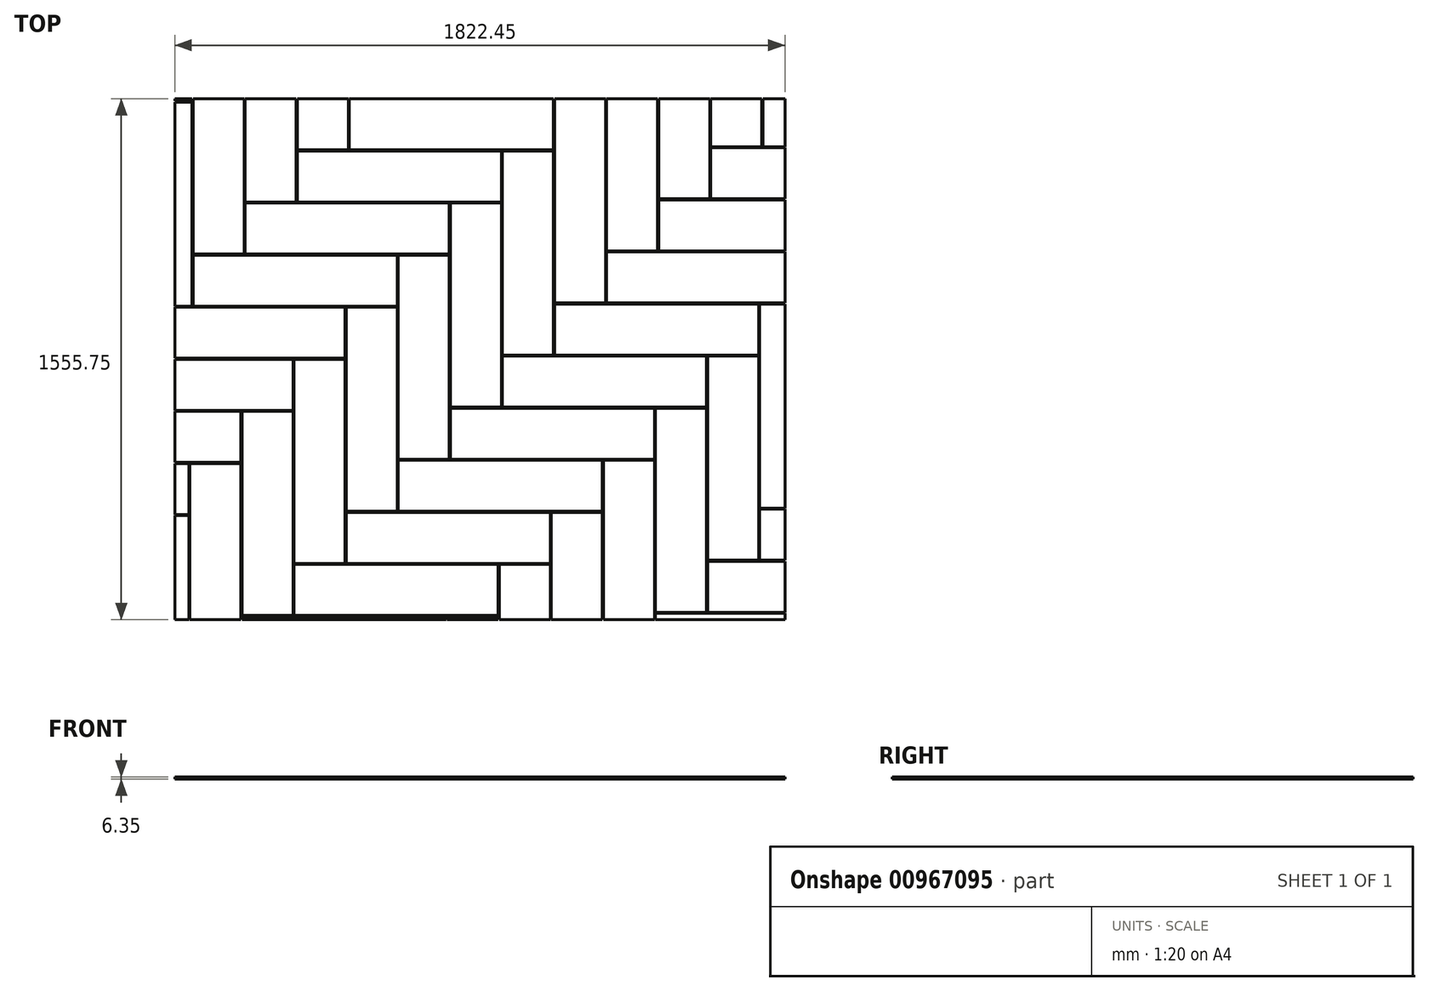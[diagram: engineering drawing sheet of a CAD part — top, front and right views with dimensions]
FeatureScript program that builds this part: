
annotation { "Feature Type Name" : "Feature", "Feature Type Description" : "" }
export const myFeature = defineFeature(function(context is Context, id is Id, definition is map)
    precondition{}
    {
        {
            var Q0;
            Q0=qCreatedBy(makeId("Top.planeOp"),FACE);
            var sketch = newSketch(context, id + "F0", { "sketchPlane" : qUnion([Q0])});
            skLineSegment(sketch, "E0.bottom", {"start": v(0, 0) * mm, "end": v(609.6, 0) * mm});
            skLineSegment(sketch, "E0.top", {"start": v(0, 152.4) * mm, "end": v(609.6, 152.4) * mm});
            skLineSegment(sketch, "E0.left", {"start": v(0, 0) * mm, "end": v(0, 152.4) * mm});
            skLineSegment(sketch, "E0.right", {"start": v(609.6, 0) * mm, "end": v(609.6, 152.4) * mm});
            skLineSegment(sketch, "E1.bottom", {"start": v(152.4, 155.57) * mm, "end": v(152.4, 765.17) * mm});
            skLineSegment(sketch, "E1.top", {"start": v(0, 155.58) * mm, "end": v(0, 765.17) * mm});
            skLineSegment(sketch, "E1.left", {"start": v(152.4, 155.57) * mm, "end": v(0, 155.57) * mm});
            skLineSegment(sketch, "E1.right", {"start": v(152.4, 765.17) * mm, "end": v(0, 765.17) * mm});
            skLineSegment(sketch, "E2.bottom", {"start": v(155.58, 155.57) * mm, "end": v(765.17, 155.57) * mm});
            skLineSegment(sketch, "E2.top", {"start": v(155.58, 307.98) * mm, "end": v(765.17, 307.97) * mm});
            skLineSegment(sketch, "E2.left", {"start": v(155.58, 155.58) * mm, "end": v(155.58, 307.98) * mm});
            skLineSegment(sketch, "E2.right", {"start": v(765.17, 155.57) * mm, "end": v(765.17, 307.97) * mm});
            skLineSegment(sketch, "E3.bottom", {"start": v(307.98, 311.15) * mm, "end": v(307.98, 920.75) * mm});
            skLineSegment(sketch, "E3.top", {"start": v(155.58, 311.15) * mm, "end": v(155.58, 920.75) * mm});
            skLineSegment(sketch, "E3.left", {"start": v(307.98, 311.15) * mm, "end": v(155.58, 311.15) * mm});
            skLineSegment(sketch, "E3.right", {"start": v(307.98, 920.75) * mm, "end": v(155.58, 920.75) * mm});
            skLineSegment(sketch, "E4.0.1.0", {"start": v(-612.78, 612.78) * mm, "end": v(-3.18, 612.78) * mm});
            skLineSegment(sketch, "E4.0.1.1", {"start": v(-460.37, 768.35) * mm, "end": v(-612.77, 768.35) * mm});
            skLineSegment(sketch, "E4.0.1.2", {"start": v(-457.2, 768.35) * mm, "end": v(-457.2, 920.75) * mm});
            skLineSegment(sketch, "E4.0.1.3", {"start": v(-304.8, 923.92) * mm, "end": v(-457.2, 923.92) * mm});
            skLineSegment(sketch, "E4.0.1.4", {"start": v(-457.2, 768.35) * mm, "end": v(152.4, 768.35) * mm});
            skLineSegment(sketch, "E4.0.1.5", {"start": v(-460.37, 768.35) * mm, "end": v(-460.37, 1377.95) * mm});
            skLineSegment(sketch, "E4.0.1.6", {"start": v(-457.2, 920.75) * mm, "end": v(152.4, 920.75) * mm});
            skLineSegment(sketch, "E4.0.1.7", {"start": v(-304.8, 1533.52) * mm, "end": v(-457.2, 1533.52) * mm});
            skLineSegment(sketch, "E4.0.1.8", {"start": v(-612.78, 768.35) * mm, "end": v(-612.77, 1377.95) * mm});
            skLineSegment(sketch, "E4.0.1.9", {"start": v(-457.2, 923.92) * mm, "end": v(-457.2, 1533.52) * mm});
            skLineSegment(sketch, "E4.0.1.10", {"start": v(-3.18, 612.78) * mm, "end": v(-3.18, 765.17) * mm});
            skLineSegment(sketch, "E4.0.1.11", {"start": v(-304.8, 923.92) * mm, "end": v(-304.8, 1533.52) * mm});
            skLineSegment(sketch, "E4.0.1.12", {"start": v(-612.78, 612.78) * mm, "end": v(-612.78, 765.17) * mm});
            skLineSegment(sketch, "E4.0.1.13", {"start": v(-460.37, 1377.95) * mm, "end": v(-612.77, 1377.95) * mm});
            skLineSegment(sketch, "E4.0.1.14", {"start": v(152.4, 768.35) * mm, "end": v(152.4, 920.75) * mm});
            skLineSegment(sketch, "E4.0.1.15", {"start": v(-612.77, 765.17) * mm, "end": v(-3.17, 765.17) * mm});
            skLineSegment(sketch, "E4.1.0.0", {"start": v(311.15, 311.15) * mm, "end": v(920.75, 311.15) * mm});
            skLineSegment(sketch, "E4.1.0.1", {"start": v(463.55, 466.72) * mm, "end": v(311.15, 466.72) * mm});
            skLineSegment(sketch, "E4.1.0.2", {"start": v(466.73, 466.72) * mm, "end": v(466.73, 619.12) * mm});
            skLineSegment(sketch, "E4.1.0.3", {"start": v(619.13, 622.3) * mm, "end": v(466.73, 622.3) * mm});
            skLineSegment(sketch, "E4.1.0.4", {"start": v(466.73, 466.72) * mm, "end": v(1076.33, 466.72) * mm});
            skLineSegment(sketch, "E4.1.0.5", {"start": v(463.55, 466.72) * mm, "end": v(463.55, 1076.32) * mm});
            skLineSegment(sketch, "E4.1.0.6", {"start": v(466.73, 619.12) * mm, "end": v(1076.33, 619.12) * mm});
            skLineSegment(sketch, "E4.1.0.7", {"start": v(619.13, 1231.9) * mm, "end": v(466.73, 1231.9) * mm});
            skLineSegment(sketch, "E4.1.0.8", {"start": v(311.15, 466.72) * mm, "end": v(311.15, 1076.32) * mm});
            skLineSegment(sketch, "E4.1.0.9", {"start": v(466.73, 622.3) * mm, "end": v(466.73, 1231.9) * mm});
            skLineSegment(sketch, "E4.1.0.10", {"start": v(920.75, 311.15) * mm, "end": v(920.75, 463.55) * mm});
            skLineSegment(sketch, "E4.1.0.11", {"start": v(619.13, 622.3) * mm, "end": v(619.13, 1231.9) * mm});
            skLineSegment(sketch, "E4.1.0.12", {"start": v(311.15, 311.15) * mm, "end": v(311.15, 463.55) * mm});
            skLineSegment(sketch, "E4.1.0.13", {"start": v(463.55, 1076.32) * mm, "end": v(311.15, 1076.32) * mm});
            skLineSegment(sketch, "E4.1.0.14", {"start": v(1076.32, 466.72) * mm, "end": v(1076.32, 619.12) * mm});
            skLineSegment(sketch, "E4.1.0.15", {"start": v(311.15, 463.55) * mm, "end": v(920.75, 463.55) * mm});
            skLineSegment(sketch, "E4.1.1.0", {"start": v(-301.62, 923.92) * mm, "end": v(307.98, 923.92) * mm});
            skLineSegment(sketch, "E4.1.1.1", {"start": v(-149.22, 1079.5) * mm, "end": v(-301.62, 1079.5) * mm});
            skLineSegment(sketch, "E4.1.1.2", {"start": v(-146.05, 1079.5) * mm, "end": v(-146.05, 1231.9) * mm});
            skLineSegment(sketch, "E4.1.1.3", {"start": v(6.35, 1235.07) * mm, "end": v(-146.05, 1235.07) * mm});
            skLineSegment(sketch, "E4.1.1.4", {"start": v(-146.05, 1079.5) * mm, "end": v(463.55, 1079.5) * mm});
            skLineSegment(sketch, "E4.1.1.5", {"start": v(-149.22, 1079.5) * mm, "end": v(-149.22, 1689.1) * mm});
            skLineSegment(sketch, "E4.1.1.6", {"start": v(-146.05, 1231.9) * mm, "end": v(463.55, 1231.9) * mm});
            skLineSegment(sketch, "E4.1.1.7", {"start": v(6.35, 1844.67) * mm, "end": v(-146.05, 1844.67) * mm});
            skLineSegment(sketch, "E4.1.1.8", {"start": v(-301.62, 1079.5) * mm, "end": v(-301.62, 1689.1) * mm});
            skLineSegment(sketch, "E4.1.1.9", {"start": v(-146.05, 1235.07) * mm, "end": v(-146.05, 1844.67) * mm});
            skLineSegment(sketch, "E4.1.1.10", {"start": v(307.98, 923.92) * mm, "end": v(307.98, 1076.32) * mm});
            skLineSegment(sketch, "E4.1.1.11", {"start": v(6.35, 1235.07) * mm, "end": v(6.35, 1844.67) * mm});
            skLineSegment(sketch, "E4.1.1.12", {"start": v(-301.62, 923.92) * mm, "end": v(-301.62, 1076.32) * mm});
            skLineSegment(sketch, "E4.1.1.13", {"start": v(-149.22, 1689.1) * mm, "end": v(-301.62, 1689.1) * mm});
            skLineSegment(sketch, "E4.1.1.14", {"start": v(463.55, 1079.5) * mm, "end": v(463.55, 1231.9) * mm});
            skLineSegment(sketch, "E4.1.1.15", {"start": v(-301.62, 1076.32) * mm, "end": v(307.98, 1076.32) * mm});
            skLineSegment(sketch, "E4.2.0.0", {"start": v(622.3, 622.3) * mm, "end": v(1231.9, 622.3) * mm});
            skLineSegment(sketch, "E4.2.0.1", {"start": v(774.7, 777.87) * mm, "end": v(622.3, 777.87) * mm});
            skLineSegment(sketch, "E4.2.0.2", {"start": v(777.88, 777.87) * mm, "end": v(777.88, 930.27) * mm});
            skLineSegment(sketch, "E4.2.0.3", {"start": v(930.28, 933.45) * mm, "end": v(777.88, 933.45) * mm});
            skLineSegment(sketch, "E4.2.0.4", {"start": v(777.88, 777.87) * mm, "end": v(1387.47, 777.87) * mm});
            skLineSegment(sketch, "E4.2.0.5", {"start": v(774.7, 777.87) * mm, "end": v(774.7, 1387.47) * mm});
            skLineSegment(sketch, "E4.2.0.6", {"start": v(777.88, 930.27) * mm, "end": v(1387.47, 930.27) * mm});
            skLineSegment(sketch, "E4.2.0.7", {"start": v(930.28, 1543.05) * mm, "end": v(777.88, 1543.05) * mm});
            skLineSegment(sketch, "E4.2.0.8", {"start": v(622.3, 777.87) * mm, "end": v(622.3, 1387.47) * mm});
            skLineSegment(sketch, "E4.2.0.9", {"start": v(777.88, 933.45) * mm, "end": v(777.88, 1543.05) * mm});
            skLineSegment(sketch, "E4.2.0.10", {"start": v(1231.9, 622.3) * mm, "end": v(1231.9, 774.7) * mm});
            skLineSegment(sketch, "E4.2.0.11", {"start": v(930.28, 933.45) * mm, "end": v(930.28, 1543.05) * mm});
            skLineSegment(sketch, "E4.2.0.12", {"start": v(622.3, 622.3) * mm, "end": v(622.3, 774.7) * mm});
            skLineSegment(sketch, "E4.2.0.13", {"start": v(774.7, 1387.47) * mm, "end": v(622.3, 1387.47) * mm});
            skLineSegment(sketch, "E4.2.0.14", {"start": v(1387.47, 777.87) * mm, "end": v(1387.47, 930.27) * mm});
            skLineSegment(sketch, "E4.2.0.15", {"start": v(622.3, 774.7) * mm, "end": v(1231.9, 774.7) * mm});
            skLineSegment(sketch, "E4.2.1.0", {"start": v(9.53, 1235.07) * mm, "end": v(619.13, 1235.07) * mm});
            skLineSegment(sketch, "E4.2.1.1", {"start": v(161.93, 1390.65) * mm, "end": v(9.53, 1390.65) * mm});
            skLineSegment(sketch, "E4.2.1.2", {"start": v(165.1, 1390.65) * mm, "end": v(165.1, 1543.05) * mm});
            skLineSegment(sketch, "E4.2.1.3", {"start": v(317.5, 1546.22) * mm, "end": v(165.1, 1546.22) * mm});
            skLineSegment(sketch, "E4.2.1.4", {"start": v(165.1, 1390.65) * mm, "end": v(774.7, 1390.65) * mm});
            skLineSegment(sketch, "E4.2.1.5", {"start": v(161.93, 1390.65) * mm, "end": v(161.93, 2000.25) * mm});
            skLineSegment(sketch, "E4.2.1.6", {"start": v(165.1, 1543.05) * mm, "end": v(774.7, 1543.05) * mm});
            skLineSegment(sketch, "E4.2.1.7", {"start": v(317.5, 2155.82) * mm, "end": v(165.1, 2155.82) * mm});
            skLineSegment(sketch, "E4.2.1.8", {"start": v(9.53, 1390.65) * mm, "end": v(9.53, 2000.25) * mm});
            skLineSegment(sketch, "E4.2.1.9", {"start": v(165.1, 1546.22) * mm, "end": v(165.1, 2155.82) * mm});
            skLineSegment(sketch, "E4.2.1.10", {"start": v(619.13, 1235.07) * mm, "end": v(619.13, 1387.47) * mm});
            skLineSegment(sketch, "E4.2.1.11", {"start": v(317.5, 1546.22) * mm, "end": v(317.5, 2155.82) * mm});
            skLineSegment(sketch, "E4.2.1.12", {"start": v(9.53, 1235.07) * mm, "end": v(9.53, 1387.47) * mm});
            skLineSegment(sketch, "E4.2.1.13", {"start": v(161.93, 2000.25) * mm, "end": v(9.53, 2000.25) * mm});
            skLineSegment(sketch, "E4.2.1.14", {"start": v(774.7, 1390.65) * mm, "end": v(774.7, 1543.05) * mm});
            skLineSegment(sketch, "E4.2.1.15", {"start": v(9.53, 1387.47) * mm, "end": v(619.13, 1387.47) * mm});
            skLineSegment(sketch, "E4.direction1", {"start": v(0, 0) * mm, "end": v(311.15, 311.15) * mm, "construction": true});
            skLineSegment(sketch, "E4.direction2", {"start": v(0, 0) * mm, "end": v(-612.78, 612.78) * mm, "construction": true});
            skLineSegment(sketch, "E5.0.3.0", {"start": v(933.45, 933.45) * mm, "end": v(1543.05, 933.45) * mm});
            skLineSegment(sketch, "E5.3.3.0", {"start": v(1085.85, 1089.02) * mm, "end": v(933.45, 1089.02) * mm});
            skLineSegment(sketch, "E5.6.3.0", {"start": v(1089.03, 1089.02) * mm, "end": v(1089.03, 1241.42) * mm});
            skLineSegment(sketch, "E5.9.3.0", {"start": v(1241.43, 1244.6) * mm, "end": v(1089.03, 1244.6) * mm});
            skLineSegment(sketch, "E5.12.3.0", {"start": v(1089.03, 1089.02) * mm, "end": v(1698.62, 1089.02) * mm});
            skLineSegment(sketch, "E5.15.3.0", {"start": v(1085.85, 1089.02) * mm, "end": v(1085.85, 1698.62) * mm});
            skLineSegment(sketch, "E5.18.3.0", {"start": v(1089.03, 1241.42) * mm, "end": v(1698.62, 1241.42) * mm});
            skLineSegment(sketch, "E5.21.3.0", {"start": v(1241.43, 1854.2) * mm, "end": v(1089.03, 1854.2) * mm});
            skLineSegment(sketch, "E5.24.3.0", {"start": v(933.45, 1089.02) * mm, "end": v(933.45, 1698.62) * mm});
            skLineSegment(sketch, "E5.27.3.0", {"start": v(1089.03, 1244.6) * mm, "end": v(1089.03, 1854.2) * mm});
            skLineSegment(sketch, "E5.30.3.0", {"start": v(1543.05, 933.45) * mm, "end": v(1543.05, 1085.85) * mm});
            skLineSegment(sketch, "E5.33.3.0", {"start": v(1241.43, 1244.6) * mm, "end": v(1241.43, 1854.2) * mm});
            skLineSegment(sketch, "E5.36.3.0", {"start": v(933.45, 933.45) * mm, "end": v(933.45, 1085.85) * mm});
            skLineSegment(sketch, "E5.39.3.0", {"start": v(1085.85, 1698.62) * mm, "end": v(933.45, 1698.62) * mm});
            skLineSegment(sketch, "E5.42.3.0", {"start": v(1698.62, 1089.02) * mm, "end": v(1698.62, 1241.42) * mm});
            skLineSegment(sketch, "E5.45.3.0", {"start": v(933.45, 1085.85) * mm, "end": v(1543.05, 1085.85) * mm});
            skLineSegment(sketch, "E5.0.3.1", {"start": v(320.68, 1546.22) * mm, "end": v(930.28, 1546.22) * mm});
            skLineSegment(sketch, "E5.3.3.1", {"start": v(473.08, 1701.8) * mm, "end": v(320.68, 1701.8) * mm});
            skLineSegment(sketch, "E5.6.3.1", {"start": v(476.25, 1701.8) * mm, "end": v(476.25, 1854.2) * mm});
            skLineSegment(sketch, "E5.9.3.1", {"start": v(628.65, 1857.37) * mm, "end": v(476.25, 1857.37) * mm});
            skLineSegment(sketch, "E5.12.3.1", {"start": v(476.25, 1701.8) * mm, "end": v(1085.85, 1701.8) * mm});
            skLineSegment(sketch, "E5.15.3.1", {"start": v(473.08, 1701.8) * mm, "end": v(473.08, 2311.4) * mm});
            skLineSegment(sketch, "E5.18.3.1", {"start": v(476.25, 1854.2) * mm, "end": v(1085.85, 1854.2) * mm});
            skLineSegment(sketch, "E5.21.3.1", {"start": v(628.65, 2466.97) * mm, "end": v(476.25, 2466.97) * mm});
            skLineSegment(sketch, "E5.24.3.1", {"start": v(320.68, 1701.8) * mm, "end": v(320.68, 2311.4) * mm});
            skLineSegment(sketch, "E5.27.3.1", {"start": v(476.25, 1857.37) * mm, "end": v(476.25, 2466.97) * mm});
            skLineSegment(sketch, "E5.30.3.1", {"start": v(930.28, 1546.22) * mm, "end": v(930.28, 1698.62) * mm});
            skLineSegment(sketch, "E5.33.3.1", {"start": v(628.65, 1857.37) * mm, "end": v(628.65, 2466.97) * mm});
            skLineSegment(sketch, "E5.36.3.1", {"start": v(320.68, 1546.22) * mm, "end": v(320.68, 1698.62) * mm});
            skLineSegment(sketch, "E5.39.3.1", {"start": v(473.08, 2311.4) * mm, "end": v(320.68, 2311.4) * mm});
            skLineSegment(sketch, "E5.42.3.1", {"start": v(1085.85, 1701.8) * mm, "end": v(1085.85, 1854.2) * mm});
            skLineSegment(sketch, "E5.45.3.1", {"start": v(320.68, 1698.62) * mm, "end": v(930.28, 1698.62) * mm});
            skLineSegment(sketch, "E5.0.4.0", {"start": v(1244.6, 1244.6) * mm, "end": v(1854.2, 1244.6) * mm});
            skLineSegment(sketch, "E5.3.4.0", {"start": v(1397, 1400.17) * mm, "end": v(1244.6, 1400.17) * mm});
            skLineSegment(sketch, "E5.6.4.0", {"start": v(1400.18, 1400.17) * mm, "end": v(1400.18, 1552.57) * mm});
            skLineSegment(sketch, "E5.9.4.0", {"start": v(1552.58, 1555.75) * mm, "end": v(1400.18, 1555.75) * mm});
            skLineSegment(sketch, "E5.12.4.0", {"start": v(1400.18, 1400.17) * mm, "end": v(2009.78, 1400.17) * mm});
            skLineSegment(sketch, "E5.15.4.0", {"start": v(1397, 1400.17) * mm, "end": v(1397, 2009.77) * mm});
            skLineSegment(sketch, "E5.18.4.0", {"start": v(1400.18, 1552.57) * mm, "end": v(2009.78, 1552.57) * mm});
            skLineSegment(sketch, "E5.21.4.0", {"start": v(1552.58, 2165.35) * mm, "end": v(1400.18, 2165.35) * mm});
            skLineSegment(sketch, "E5.24.4.0", {"start": v(1244.6, 1400.17) * mm, "end": v(1244.6, 2009.77) * mm});
            skLineSegment(sketch, "E5.27.4.0", {"start": v(1400.18, 1555.75) * mm, "end": v(1400.18, 2165.35) * mm});
            skLineSegment(sketch, "E5.30.4.0", {"start": v(1854.2, 1244.6) * mm, "end": v(1854.2, 1397) * mm});
            skLineSegment(sketch, "E5.33.4.0", {"start": v(1552.58, 1555.75) * mm, "end": v(1552.58, 2165.35) * mm});
            skLineSegment(sketch, "E5.36.4.0", {"start": v(1244.6, 1244.6) * mm, "end": v(1244.6, 1397) * mm});
            skLineSegment(sketch, "E5.39.4.0", {"start": v(1397, 2009.77) * mm, "end": v(1244.6, 2009.77) * mm});
            skLineSegment(sketch, "E5.42.4.0", {"start": v(2009.78, 1400.17) * mm, "end": v(2009.78, 1552.57) * mm});
            skLineSegment(sketch, "E5.45.4.0", {"start": v(1244.6, 1397) * mm, "end": v(1854.2, 1397) * mm});
            skLineSegment(sketch, "E5.0.4.1", {"start": v(631.83, 1857.37) * mm, "end": v(1241.43, 1857.37) * mm});
            skLineSegment(sketch, "E5.3.4.1", {"start": v(784.23, 2012.95) * mm, "end": v(631.83, 2012.95) * mm});
            skLineSegment(sketch, "E5.6.4.1", {"start": v(787.4, 2012.95) * mm, "end": v(787.4, 2165.35) * mm});
            skLineSegment(sketch, "E5.9.4.1", {"start": v(939.8, 2168.52) * mm, "end": v(787.4, 2168.52) * mm});
            skLineSegment(sketch, "E5.12.4.1", {"start": v(787.4, 2012.95) * mm, "end": v(1397, 2012.95) * mm});
            skLineSegment(sketch, "E5.15.4.1", {"start": v(784.23, 2012.95) * mm, "end": v(784.23, 2622.55) * mm});
            skLineSegment(sketch, "E5.18.4.1", {"start": v(787.4, 2165.35) * mm, "end": v(1397, 2165.35) * mm});
            skLineSegment(sketch, "E5.21.4.1", {"start": v(939.8, 2778.12) * mm, "end": v(787.4, 2778.12) * mm});
            skLineSegment(sketch, "E5.24.4.1", {"start": v(631.83, 2012.95) * mm, "end": v(631.83, 2622.55) * mm});
            skLineSegment(sketch, "E5.27.4.1", {"start": v(787.4, 2168.52) * mm, "end": v(787.4, 2778.12) * mm});
            skLineSegment(sketch, "E5.30.4.1", {"start": v(1241.43, 1857.37) * mm, "end": v(1241.43, 2009.77) * mm});
            skLineSegment(sketch, "E5.33.4.1", {"start": v(939.8, 2168.52) * mm, "end": v(939.8, 2778.12) * mm});
            skLineSegment(sketch, "E5.36.4.1", {"start": v(631.83, 1857.37) * mm, "end": v(631.83, 2009.77) * mm});
            skLineSegment(sketch, "E5.39.4.1", {"start": v(784.23, 2622.55) * mm, "end": v(631.83, 2622.55) * mm});
            skLineSegment(sketch, "E5.42.4.1", {"start": v(1397, 2012.95) * mm, "end": v(1397, 2165.35) * mm});
            skLineSegment(sketch, "E5.45.4.1", {"start": v(631.83, 2009.77) * mm, "end": v(1241.43, 2009.77) * mm});
            skLineSegment(sketch, "E5.0.5.0", {"start": v(1555.75, 1555.75) * mm, "end": v(2165.35, 1555.75) * mm});
            skLineSegment(sketch, "E5.3.5.0", {"start": v(1708.15, 1711.32) * mm, "end": v(1555.75, 1711.32) * mm});
            skLineSegment(sketch, "E5.6.5.0", {"start": v(1711.33, 1711.32) * mm, "end": v(1711.33, 1863.72) * mm});
            skLineSegment(sketch, "E5.9.5.0", {"start": v(1863.73, 1866.9) * mm, "end": v(1711.33, 1866.9) * mm});
            skLineSegment(sketch, "E5.12.5.0", {"start": v(1711.33, 1711.32) * mm, "end": v(2320.92, 1711.32) * mm});
            skLineSegment(sketch, "E5.15.5.0", {"start": v(1708.15, 1711.32) * mm, "end": v(1708.15, 2320.92) * mm});
            skLineSegment(sketch, "E5.18.5.0", {"start": v(1711.33, 1863.72) * mm, "end": v(2320.92, 1863.72) * mm});
            skLineSegment(sketch, "E5.21.5.0", {"start": v(1863.73, 2476.5) * mm, "end": v(1711.33, 2476.5) * mm});
            skLineSegment(sketch, "E5.24.5.0", {"start": v(1555.75, 1711.32) * mm, "end": v(1555.75, 2320.92) * mm});
            skLineSegment(sketch, "E5.27.5.0", {"start": v(1711.33, 1866.9) * mm, "end": v(1711.33, 2476.5) * mm});
            skLineSegment(sketch, "E5.30.5.0", {"start": v(2165.35, 1555.75) * mm, "end": v(2165.35, 1708.15) * mm});
            skLineSegment(sketch, "E5.33.5.0", {"start": v(1863.73, 1866.9) * mm, "end": v(1863.73, 2476.5) * mm});
            skLineSegment(sketch, "E5.36.5.0", {"start": v(1555.75, 1555.75) * mm, "end": v(1555.75, 1708.15) * mm});
            skLineSegment(sketch, "E5.39.5.0", {"start": v(1708.15, 2320.92) * mm, "end": v(1555.75, 2320.92) * mm});
            skLineSegment(sketch, "E5.42.5.0", {"start": v(2320.92, 1711.32) * mm, "end": v(2320.92, 1863.72) * mm});
            skLineSegment(sketch, "E5.45.5.0", {"start": v(1555.75, 1708.15) * mm, "end": v(2165.35, 1708.15) * mm});
            skLineSegment(sketch, "E5.0.5.1", {"start": v(942.98, 2168.52) * mm, "end": v(1552.58, 2168.52) * mm});
            skLineSegment(sketch, "E5.3.5.1", {"start": v(1095.38, 2324.1) * mm, "end": v(942.98, 2324.1) * mm});
            skLineSegment(sketch, "E5.6.5.1", {"start": v(1098.55, 2324.1) * mm, "end": v(1098.55, 2476.5) * mm});
            skLineSegment(sketch, "E5.9.5.1", {"start": v(1250.95, 2479.67) * mm, "end": v(1098.55, 2479.67) * mm});
            skLineSegment(sketch, "E5.12.5.1", {"start": v(1098.55, 2324.1) * mm, "end": v(1708.15, 2324.1) * mm});
            skLineSegment(sketch, "E5.15.5.1", {"start": v(1095.38, 2324.1) * mm, "end": v(1095.38, 2933.7) * mm});
            skLineSegment(sketch, "E5.18.5.1", {"start": v(1098.55, 2476.5) * mm, "end": v(1708.15, 2476.5) * mm});
            skLineSegment(sketch, "E5.21.5.1", {"start": v(1250.95, 3089.27) * mm, "end": v(1098.55, 3089.27) * mm});
            skLineSegment(sketch, "E5.24.5.1", {"start": v(942.98, 2324.1) * mm, "end": v(942.98, 2933.7) * mm});
            skLineSegment(sketch, "E5.27.5.1", {"start": v(1098.55, 2479.67) * mm, "end": v(1098.55, 3089.27) * mm});
            skLineSegment(sketch, "E5.30.5.1", {"start": v(1552.58, 2168.52) * mm, "end": v(1552.58, 2320.92) * mm});
            skLineSegment(sketch, "E5.33.5.1", {"start": v(1250.95, 2479.67) * mm, "end": v(1250.95, 3089.27) * mm});
            skLineSegment(sketch, "E5.36.5.1", {"start": v(942.98, 2168.52) * mm, "end": v(942.98, 2320.92) * mm});
            skLineSegment(sketch, "E5.39.5.1", {"start": v(1095.38, 2933.7) * mm, "end": v(942.98, 2933.7) * mm});
            skLineSegment(sketch, "E5.42.5.1", {"start": v(1708.15, 2324.1) * mm, "end": v(1708.15, 2476.5) * mm});
            skLineSegment(sketch, "E5.45.5.1", {"start": v(942.98, 2320.92) * mm, "end": v(1552.58, 2320.92) * mm});
            skLineSegment(sketch, "E6.0.0.2", {"start": v(-1225.55, 1225.55) * mm, "end": v(-615.95, 1225.55) * mm});
            skLineSegment(sketch, "E6.3.0.2", {"start": v(-1073.15, 1381.12) * mm, "end": v(-1225.55, 1381.12) * mm});
            skLineSegment(sketch, "E6.6.0.2", {"start": v(-1069.97, 1381.12) * mm, "end": v(-1069.97, 1533.52) * mm});
            skLineSegment(sketch, "E6.9.0.2", {"start": v(-917.57, 1536.7) * mm, "end": v(-1069.97, 1536.7) * mm});
            skLineSegment(sketch, "E6.12.0.2", {"start": v(-1069.97, 1381.12) * mm, "end": v(-460.37, 1381.12) * mm});
            skLineSegment(sketch, "E6.15.0.2", {"start": v(-1073.15, 1381.12) * mm, "end": v(-1073.15, 1990.72) * mm});
            skLineSegment(sketch, "E6.18.0.2", {"start": v(-1069.97, 1533.52) * mm, "end": v(-460.37, 1533.52) * mm});
            skLineSegment(sketch, "E6.21.0.2", {"start": v(-917.57, 2146.3) * mm, "end": v(-1069.97, 2146.3) * mm});
            skLineSegment(sketch, "E6.24.0.2", {"start": v(-1225.55, 1381.12) * mm, "end": v(-1225.55, 1990.72) * mm});
            skLineSegment(sketch, "E6.27.0.2", {"start": v(-1069.97, 1536.7) * mm, "end": v(-1069.97, 2146.3) * mm});
            skLineSegment(sketch, "E6.30.0.2", {"start": v(-615.95, 1225.55) * mm, "end": v(-615.95, 1377.95) * mm});
            skLineSegment(sketch, "E6.33.0.2", {"start": v(-917.57, 1536.7) * mm, "end": v(-917.57, 2146.3) * mm});
            skLineSegment(sketch, "E6.36.0.2", {"start": v(-1225.55, 1225.55) * mm, "end": v(-1225.55, 1377.95) * mm});
            skLineSegment(sketch, "E6.39.0.2", {"start": v(-1073.15, 1990.72) * mm, "end": v(-1225.55, 1990.72) * mm});
            skLineSegment(sketch, "E6.42.0.2", {"start": v(-460.37, 1381.12) * mm, "end": v(-460.37, 1533.52) * mm});
            skLineSegment(sketch, "E6.45.0.2", {"start": v(-1225.55, 1377.95) * mm, "end": v(-615.95, 1377.95) * mm});
            skLineSegment(sketch, "E6.0.0.3", {"start": v(-1838.33, 1838.33) * mm, "end": v(-1228.73, 1838.33) * mm});
            skLineSegment(sketch, "E6.3.0.3", {"start": v(-1685.92, 1993.9) * mm, "end": v(-1838.32, 1993.9) * mm});
            skLineSegment(sketch, "E6.6.0.3", {"start": v(-1682.75, 1993.9) * mm, "end": v(-1682.75, 2146.3) * mm});
            skLineSegment(sketch, "E6.9.0.3", {"start": v(-1530.35, 2149.47) * mm, "end": v(-1682.75, 2149.47) * mm});
            skLineSegment(sketch, "E6.12.0.3", {"start": v(-1682.75, 1993.9) * mm, "end": v(-1073.15, 1993.9) * mm});
            skLineSegment(sketch, "E6.15.0.3", {"start": v(-1685.92, 1993.9) * mm, "end": v(-1685.92, 2603.5) * mm});
            skLineSegment(sketch, "E6.18.0.3", {"start": v(-1682.75, 2146.3) * mm, "end": v(-1073.15, 2146.3) * mm});
            skLineSegment(sketch, "E6.21.0.3", {"start": v(-1530.35, 2759.07) * mm, "end": v(-1682.75, 2759.07) * mm});
            skLineSegment(sketch, "E6.24.0.3", {"start": v(-1838.33, 1993.9) * mm, "end": v(-1838.33, 2603.5) * mm});
            skLineSegment(sketch, "E6.27.0.3", {"start": v(-1682.75, 2149.47) * mm, "end": v(-1682.75, 2759.07) * mm});
            skLineSegment(sketch, "E6.30.0.3", {"start": v(-1228.73, 1838.33) * mm, "end": v(-1228.73, 1990.72) * mm});
            skLineSegment(sketch, "E6.33.0.3", {"start": v(-1530.35, 2149.47) * mm, "end": v(-1530.35, 2759.07) * mm});
            skLineSegment(sketch, "E6.36.0.3", {"start": v(-1838.33, 1838.33) * mm, "end": v(-1838.33, 1990.72) * mm});
            skLineSegment(sketch, "E6.39.0.3", {"start": v(-1685.92, 2603.5) * mm, "end": v(-1838.32, 2603.5) * mm});
            skLineSegment(sketch, "E6.42.0.3", {"start": v(-1073.15, 1993.9) * mm, "end": v(-1073.15, 2146.3) * mm});
            skLineSegment(sketch, "E6.45.0.3", {"start": v(-1838.32, 1990.72) * mm, "end": v(-1228.72, 1990.72) * mm});
            skLineSegment(sketch, "E6.0.0.4", {"start": v(-2451.1, 2451.1) * mm, "end": v(-1841.5, 2451.1) * mm});
            skLineSegment(sketch, "E6.3.0.4", {"start": v(-2298.7, 2606.67) * mm, "end": v(-2451.1, 2606.67) * mm});
            skLineSegment(sketch, "E6.6.0.4", {"start": v(-2295.52, 2606.67) * mm, "end": v(-2295.52, 2759.07) * mm});
            skLineSegment(sketch, "E6.9.0.4", {"start": v(-2143.12, 2762.25) * mm, "end": v(-2295.52, 2762.25) * mm});
            skLineSegment(sketch, "E6.12.0.4", {"start": v(-2295.52, 2606.67) * mm, "end": v(-1685.92, 2606.67) * mm});
            skLineSegment(sketch, "E6.15.0.4", {"start": v(-2298.7, 2606.67) * mm, "end": v(-2298.7, 3216.27) * mm});
            skLineSegment(sketch, "E6.18.0.4", {"start": v(-2295.52, 2759.07) * mm, "end": v(-1685.92, 2759.07) * mm});
            skLineSegment(sketch, "E6.21.0.4", {"start": v(-2143.12, 3371.85) * mm, "end": v(-2295.52, 3371.85) * mm});
            skLineSegment(sketch, "E6.24.0.4", {"start": v(-2451.1, 2606.67) * mm, "end": v(-2451.1, 3216.27) * mm});
            skLineSegment(sketch, "E6.27.0.4", {"start": v(-2295.52, 2762.25) * mm, "end": v(-2295.52, 3371.85) * mm});
            skLineSegment(sketch, "E6.30.0.4", {"start": v(-1841.5, 2451.1) * mm, "end": v(-1841.5, 2603.5) * mm});
            skLineSegment(sketch, "E6.33.0.4", {"start": v(-2143.12, 2762.25) * mm, "end": v(-2143.12, 3371.85) * mm});
            skLineSegment(sketch, "E6.36.0.4", {"start": v(-2451.1, 2451.1) * mm, "end": v(-2451.1, 2603.5) * mm});
            skLineSegment(sketch, "E6.39.0.4", {"start": v(-2298.7, 3216.27) * mm, "end": v(-2451.1, 3216.27) * mm});
            skLineSegment(sketch, "E6.42.0.4", {"start": v(-1685.92, 2606.67) * mm, "end": v(-1685.92, 2759.07) * mm});
            skLineSegment(sketch, "E6.45.0.4", {"start": v(-2451.1, 2603.5) * mm, "end": v(-1841.5, 2603.5) * mm});
            skLineSegment(sketch, "E6.0.1.2", {"start": v(-914.4, 1536.7) * mm, "end": v(-304.8, 1536.7) * mm});
            skLineSegment(sketch, "E6.3.1.2", {"start": v(-762, 1692.27) * mm, "end": v(-914.4, 1692.27) * mm});
            skLineSegment(sketch, "E6.6.1.2", {"start": v(-758.82, 1692.27) * mm, "end": v(-758.82, 1844.67) * mm});
            skLineSegment(sketch, "E6.9.1.2", {"start": v(-606.42, 1847.85) * mm, "end": v(-758.82, 1847.85) * mm});
            skLineSegment(sketch, "E6.12.1.2", {"start": v(-758.82, 1692.27) * mm, "end": v(-149.22, 1692.27) * mm});
            skLineSegment(sketch, "E6.15.1.2", {"start": v(-762, 1692.27) * mm, "end": v(-762, 2301.87) * mm});
            skLineSegment(sketch, "E6.18.1.2", {"start": v(-758.82, 1844.67) * mm, "end": v(-149.22, 1844.67) * mm});
            skLineSegment(sketch, "E6.21.1.2", {"start": v(-606.42, 2457.45) * mm, "end": v(-758.82, 2457.45) * mm});
            skLineSegment(sketch, "E6.24.1.2", {"start": v(-914.4, 1692.27) * mm, "end": v(-914.4, 2301.87) * mm});
            skLineSegment(sketch, "E6.27.1.2", {"start": v(-758.82, 1847.85) * mm, "end": v(-758.82, 2457.45) * mm});
            skLineSegment(sketch, "E6.30.1.2", {"start": v(-304.8, 1536.7) * mm, "end": v(-304.8, 1689.1) * mm});
            skLineSegment(sketch, "E6.33.1.2", {"start": v(-606.42, 1847.85) * mm, "end": v(-606.42, 2457.45) * mm});
            skLineSegment(sketch, "E6.36.1.2", {"start": v(-914.4, 1536.7) * mm, "end": v(-914.4, 1689.1) * mm});
            skLineSegment(sketch, "E6.39.1.2", {"start": v(-762, 2301.87) * mm, "end": v(-914.4, 2301.87) * mm});
            skLineSegment(sketch, "E6.42.1.2", {"start": v(-149.22, 1692.27) * mm, "end": v(-149.22, 1844.67) * mm});
            skLineSegment(sketch, "E6.45.1.2", {"start": v(-914.4, 1689.1) * mm, "end": v(-304.8, 1689.1) * mm});
            skLineSegment(sketch, "E6.0.1.3", {"start": v(-1527.17, 2149.47) * mm, "end": v(-917.57, 2149.47) * mm});
            skLineSegment(sketch, "E6.3.1.3", {"start": v(-1374.77, 2305.05) * mm, "end": v(-1527.17, 2305.05) * mm});
            skLineSegment(sketch, "E6.6.1.3", {"start": v(-1371.6, 2305.05) * mm, "end": v(-1371.6, 2457.45) * mm});
            skLineSegment(sketch, "E6.9.1.3", {"start": v(-1219.2, 2460.62) * mm, "end": v(-1371.6, 2460.62) * mm});
            skLineSegment(sketch, "E6.12.1.3", {"start": v(-1371.6, 2305.05) * mm, "end": v(-762, 2305.05) * mm});
            skLineSegment(sketch, "E6.15.1.3", {"start": v(-1374.77, 2305.05) * mm, "end": v(-1374.77, 2914.65) * mm});
            skLineSegment(sketch, "E6.18.1.3", {"start": v(-1371.6, 2457.45) * mm, "end": v(-762, 2457.45) * mm});
            skLineSegment(sketch, "E6.21.1.3", {"start": v(-1219.2, 3070.22) * mm, "end": v(-1371.6, 3070.22) * mm});
            skLineSegment(sketch, "E6.24.1.3", {"start": v(-1527.17, 2305.05) * mm, "end": v(-1527.17, 2914.65) * mm});
            skLineSegment(sketch, "E6.27.1.3", {"start": v(-1371.6, 2460.62) * mm, "end": v(-1371.6, 3070.22) * mm});
            skLineSegment(sketch, "E6.30.1.3", {"start": v(-917.57, 2149.47) * mm, "end": v(-917.57, 2301.87) * mm});
            skLineSegment(sketch, "E6.33.1.3", {"start": v(-1219.2, 2460.62) * mm, "end": v(-1219.2, 3070.22) * mm});
            skLineSegment(sketch, "E6.36.1.3", {"start": v(-1527.17, 2149.47) * mm, "end": v(-1527.17, 2301.87) * mm});
            skLineSegment(sketch, "E6.39.1.3", {"start": v(-1374.77, 2914.65) * mm, "end": v(-1527.17, 2914.65) * mm});
            skLineSegment(sketch, "E6.42.1.3", {"start": v(-762, 2305.05) * mm, "end": v(-762, 2457.45) * mm});
            skLineSegment(sketch, "E6.45.1.3", {"start": v(-1527.17, 2301.87) * mm, "end": v(-917.57, 2301.87) * mm});
            skLineSegment(sketch, "E6.0.1.4", {"start": v(-2139.95, 2762.25) * mm, "end": v(-1530.35, 2762.25) * mm});
            skLineSegment(sketch, "E6.3.1.4", {"start": v(-1987.55, 2917.82) * mm, "end": v(-2139.95, 2917.82) * mm});
            skLineSegment(sketch, "E6.6.1.4", {"start": v(-1984.37, 2917.82) * mm, "end": v(-1984.37, 3070.22) * mm});
            skLineSegment(sketch, "E6.9.1.4", {"start": v(-1831.97, 3073.4) * mm, "end": v(-1984.37, 3073.4) * mm});
            skLineSegment(sketch, "E6.12.1.4", {"start": v(-1984.37, 2917.82) * mm, "end": v(-1374.77, 2917.82) * mm});
            skLineSegment(sketch, "E6.15.1.4", {"start": v(-1987.55, 2917.82) * mm, "end": v(-1987.55, 3527.42) * mm});
            skLineSegment(sketch, "E6.18.1.4", {"start": v(-1984.37, 3070.22) * mm, "end": v(-1374.77, 3070.22) * mm});
            skLineSegment(sketch, "E6.21.1.4", {"start": v(-1831.97, 3683) * mm, "end": v(-1984.37, 3683) * mm});
            skLineSegment(sketch, "E6.24.1.4", {"start": v(-2139.95, 2917.82) * mm, "end": v(-2139.95, 3527.42) * mm});
            skLineSegment(sketch, "E6.27.1.4", {"start": v(-1984.37, 3073.4) * mm, "end": v(-1984.37, 3683) * mm});
            skLineSegment(sketch, "E6.30.1.4", {"start": v(-1530.35, 2762.25) * mm, "end": v(-1530.35, 2914.65) * mm});
            skLineSegment(sketch, "E6.33.1.4", {"start": v(-1831.97, 3073.4) * mm, "end": v(-1831.97, 3683) * mm});
            skLineSegment(sketch, "E6.36.1.4", {"start": v(-2139.95, 2762.25) * mm, "end": v(-2139.95, 2914.65) * mm});
            skLineSegment(sketch, "E6.39.1.4", {"start": v(-1987.55, 3527.42) * mm, "end": v(-2139.95, 3527.42) * mm});
            skLineSegment(sketch, "E6.42.1.4", {"start": v(-1374.77, 2917.82) * mm, "end": v(-1374.77, 3070.22) * mm});
            skLineSegment(sketch, "E6.45.1.4", {"start": v(-2139.95, 2914.65) * mm, "end": v(-1530.35, 2914.65) * mm});
            skLineSegment(sketch, "E6.0.2.2", {"start": v(-603.25, 1847.85) * mm, "end": v(6.35, 1847.85) * mm});
            skLineSegment(sketch, "E6.3.2.2", {"start": v(-450.85, 2003.42) * mm, "end": v(-603.25, 2003.42) * mm});
            skLineSegment(sketch, "E6.6.2.2", {"start": v(-447.67, 2003.42) * mm, "end": v(-447.67, 2155.82) * mm});
            skLineSegment(sketch, "E6.9.2.2", {"start": v(-295.27, 2159) * mm, "end": v(-447.67, 2159) * mm});
            skLineSegment(sketch, "E6.12.2.2", {"start": v(-447.67, 2003.42) * mm, "end": v(161.93, 2003.42) * mm});
            skLineSegment(sketch, "E6.15.2.2", {"start": v(-450.85, 2003.42) * mm, "end": v(-450.85, 2613.02) * mm});
            skLineSegment(sketch, "E6.18.2.2", {"start": v(-447.67, 2155.82) * mm, "end": v(161.93, 2155.82) * mm});
            skLineSegment(sketch, "E6.21.2.2", {"start": v(-295.27, 2768.6) * mm, "end": v(-447.67, 2768.6) * mm});
            skLineSegment(sketch, "E6.24.2.2", {"start": v(-603.25, 2003.42) * mm, "end": v(-603.25, 2613.02) * mm});
            skLineSegment(sketch, "E6.27.2.2", {"start": v(-447.67, 2159) * mm, "end": v(-447.67, 2768.6) * mm});
            skLineSegment(sketch, "E6.30.2.2", {"start": v(6.35, 1847.85) * mm, "end": v(6.35, 2000.25) * mm});
            skLineSegment(sketch, "E6.33.2.2", {"start": v(-295.27, 2159) * mm, "end": v(-295.27, 2768.6) * mm});
            skLineSegment(sketch, "E6.36.2.2", {"start": v(-603.25, 1847.85) * mm, "end": v(-603.25, 2000.25) * mm});
            skLineSegment(sketch, "E6.39.2.2", {"start": v(-450.85, 2613.02) * mm, "end": v(-603.25, 2613.02) * mm});
            skLineSegment(sketch, "E6.42.2.2", {"start": v(161.93, 2003.42) * mm, "end": v(161.93, 2155.82) * mm});
            skLineSegment(sketch, "E6.45.2.2", {"start": v(-603.25, 2000.25) * mm, "end": v(6.35, 2000.25) * mm});
            skLineSegment(sketch, "E6.0.2.3", {"start": v(-1216.02, 2460.62) * mm, "end": v(-606.42, 2460.62) * mm});
            skLineSegment(sketch, "E6.3.2.3", {"start": v(-1063.62, 2616.2) * mm, "end": v(-1216.02, 2616.2) * mm});
            skLineSegment(sketch, "E6.6.2.3", {"start": v(-1060.45, 2616.2) * mm, "end": v(-1060.45, 2768.6) * mm});
            skLineSegment(sketch, "E6.9.2.3", {"start": v(-908.05, 2771.77) * mm, "end": v(-1060.45, 2771.77) * mm});
            skLineSegment(sketch, "E6.12.2.3", {"start": v(-1060.45, 2616.2) * mm, "end": v(-450.85, 2616.2) * mm});
            skLineSegment(sketch, "E6.15.2.3", {"start": v(-1063.62, 2616.2) * mm, "end": v(-1063.62, 3225.8) * mm});
            skLineSegment(sketch, "E6.18.2.3", {"start": v(-1060.45, 2768.6) * mm, "end": v(-450.85, 2768.6) * mm});
            skLineSegment(sketch, "E6.21.2.3", {"start": v(-908.05, 3381.37) * mm, "end": v(-1060.45, 3381.37) * mm});
            skLineSegment(sketch, "E6.24.2.3", {"start": v(-1216.02, 2616.2) * mm, "end": v(-1216.02, 3225.8) * mm});
            skLineSegment(sketch, "E6.27.2.3", {"start": v(-1060.45, 2771.77) * mm, "end": v(-1060.45, 3381.37) * mm});
            skLineSegment(sketch, "E6.30.2.3", {"start": v(-606.42, 2460.62) * mm, "end": v(-606.42, 2613.02) * mm});
            skLineSegment(sketch, "E6.33.2.3", {"start": v(-908.05, 2771.77) * mm, "end": v(-908.05, 3381.37) * mm});
            skLineSegment(sketch, "E6.36.2.3", {"start": v(-1216.02, 2460.62) * mm, "end": v(-1216.02, 2613.02) * mm});
            skLineSegment(sketch, "E6.39.2.3", {"start": v(-1063.62, 3225.8) * mm, "end": v(-1216.02, 3225.8) * mm});
            skLineSegment(sketch, "E6.42.2.3", {"start": v(-450.85, 2616.2) * mm, "end": v(-450.85, 2768.6) * mm});
            skLineSegment(sketch, "E6.45.2.3", {"start": v(-1216.02, 2613.02) * mm, "end": v(-606.42, 2613.02) * mm});
            skLineSegment(sketch, "E6.0.2.4", {"start": v(-1828.8, 3073.4) * mm, "end": v(-1219.2, 3073.4) * mm});
            skLineSegment(sketch, "E6.3.2.4", {"start": v(-1676.4, 3228.97) * mm, "end": v(-1828.8, 3228.97) * mm});
            skLineSegment(sketch, "E6.6.2.4", {"start": v(-1673.22, 3228.97) * mm, "end": v(-1673.22, 3381.37) * mm});
            skLineSegment(sketch, "E6.9.2.4", {"start": v(-1520.82, 3384.55) * mm, "end": v(-1673.22, 3384.55) * mm});
            skLineSegment(sketch, "E6.12.2.4", {"start": v(-1673.22, 3228.97) * mm, "end": v(-1063.62, 3228.97) * mm});
            skLineSegment(sketch, "E6.15.2.4", {"start": v(-1676.4, 3228.97) * mm, "end": v(-1676.4, 3838.57) * mm});
            skLineSegment(sketch, "E6.18.2.4", {"start": v(-1673.22, 3381.37) * mm, "end": v(-1063.62, 3381.37) * mm});
            skLineSegment(sketch, "E6.21.2.4", {"start": v(-1520.82, 3994.15) * mm, "end": v(-1673.22, 3994.15) * mm});
            skLineSegment(sketch, "E6.24.2.4", {"start": v(-1828.8, 3228.97) * mm, "end": v(-1828.8, 3838.57) * mm});
            skLineSegment(sketch, "E6.27.2.4", {"start": v(-1673.22, 3384.55) * mm, "end": v(-1673.22, 3994.15) * mm});
            skLineSegment(sketch, "E6.30.2.4", {"start": v(-1219.2, 3073.4) * mm, "end": v(-1219.2, 3225.8) * mm});
            skLineSegment(sketch, "E6.33.2.4", {"start": v(-1520.82, 3384.55) * mm, "end": v(-1520.82, 3994.15) * mm});
            skLineSegment(sketch, "E6.36.2.4", {"start": v(-1828.8, 3073.4) * mm, "end": v(-1828.8, 3225.8) * mm});
            skLineSegment(sketch, "E6.39.2.4", {"start": v(-1676.4, 3838.57) * mm, "end": v(-1828.8, 3838.57) * mm});
            skLineSegment(sketch, "E6.42.2.4", {"start": v(-1063.62, 3228.97) * mm, "end": v(-1063.62, 3381.37) * mm});
            skLineSegment(sketch, "E6.45.2.4", {"start": v(-1828.8, 3225.8) * mm, "end": v(-1219.2, 3225.8) * mm});
            skLineSegment(sketch, "E6.0.3.2", {"start": v(-292.1, 2159) * mm, "end": v(317.5, 2159) * mm});
            skLineSegment(sketch, "E6.3.3.2", {"start": v(-139.7, 2314.57) * mm, "end": v(-292.1, 2314.57) * mm});
            skLineSegment(sketch, "E6.6.3.2", {"start": v(-136.52, 2314.57) * mm, "end": v(-136.52, 2466.97) * mm});
            skLineSegment(sketch, "E6.9.3.2", {"start": v(15.88, 2470.15) * mm, "end": v(-136.52, 2470.15) * mm});
            skLineSegment(sketch, "E6.12.3.2", {"start": v(-136.52, 2314.57) * mm, "end": v(473.08, 2314.57) * mm});
            skLineSegment(sketch, "E6.15.3.2", {"start": v(-139.7, 2314.57) * mm, "end": v(-139.7, 2924.17) * mm});
            skLineSegment(sketch, "E6.18.3.2", {"start": v(-136.52, 2466.97) * mm, "end": v(473.08, 2466.97) * mm});
            skLineSegment(sketch, "E6.21.3.2", {"start": v(15.88, 3079.75) * mm, "end": v(-136.52, 3079.75) * mm});
            skLineSegment(sketch, "E6.24.3.2", {"start": v(-292.1, 2314.57) * mm, "end": v(-292.1, 2924.17) * mm});
            skLineSegment(sketch, "E6.27.3.2", {"start": v(-136.52, 2470.15) * mm, "end": v(-136.52, 3079.75) * mm});
            skLineSegment(sketch, "E6.30.3.2", {"start": v(317.5, 2159) * mm, "end": v(317.5, 2311.4) * mm});
            skLineSegment(sketch, "E6.33.3.2", {"start": v(15.88, 2470.15) * mm, "end": v(15.88, 3079.75) * mm});
            skLineSegment(sketch, "E6.36.3.2", {"start": v(-292.1, 2159) * mm, "end": v(-292.1, 2311.4) * mm});
            skLineSegment(sketch, "E6.39.3.2", {"start": v(-139.7, 2924.17) * mm, "end": v(-292.1, 2924.17) * mm});
            skLineSegment(sketch, "E6.42.3.2", {"start": v(473.08, 2314.57) * mm, "end": v(473.08, 2466.97) * mm});
            skLineSegment(sketch, "E6.45.3.2", {"start": v(-292.1, 2311.4) * mm, "end": v(317.5, 2311.4) * mm});
            skLineSegment(sketch, "E6.0.3.3", {"start": v(-904.87, 2771.77) * mm, "end": v(-295.27, 2771.77) * mm});
            skLineSegment(sketch, "E6.3.3.3", {"start": v(-752.47, 2927.35) * mm, "end": v(-904.87, 2927.35) * mm});
            skLineSegment(sketch, "E6.6.3.3", {"start": v(-749.3, 2927.35) * mm, "end": v(-749.3, 3079.75) * mm});
            skLineSegment(sketch, "E6.9.3.3", {"start": v(-596.9, 3082.92) * mm, "end": v(-749.3, 3082.92) * mm});
            skLineSegment(sketch, "E6.12.3.3", {"start": v(-749.3, 2927.35) * mm, "end": v(-139.7, 2927.35) * mm});
            skLineSegment(sketch, "E6.15.3.3", {"start": v(-752.47, 2927.35) * mm, "end": v(-752.47, 3536.95) * mm});
            skLineSegment(sketch, "E6.18.3.3", {"start": v(-749.3, 3079.75) * mm, "end": v(-139.7, 3079.75) * mm});
            skLineSegment(sketch, "E6.21.3.3", {"start": v(-596.9, 3692.52) * mm, "end": v(-749.3, 3692.52) * mm});
            skLineSegment(sketch, "E6.24.3.3", {"start": v(-904.87, 2927.35) * mm, "end": v(-904.87, 3536.95) * mm});
            skLineSegment(sketch, "E6.27.3.3", {"start": v(-749.3, 3082.92) * mm, "end": v(-749.3, 3692.52) * mm});
            skLineSegment(sketch, "E6.30.3.3", {"start": v(-295.27, 2771.77) * mm, "end": v(-295.27, 2924.17) * mm});
            skLineSegment(sketch, "E6.33.3.3", {"start": v(-596.9, 3082.92) * mm, "end": v(-596.9, 3692.52) * mm});
            skLineSegment(sketch, "E6.36.3.3", {"start": v(-904.87, 2771.77) * mm, "end": v(-904.87, 2924.17) * mm});
            skLineSegment(sketch, "E6.39.3.3", {"start": v(-752.47, 3536.95) * mm, "end": v(-904.87, 3536.95) * mm});
            skLineSegment(sketch, "E6.42.3.3", {"start": v(-139.7, 2927.35) * mm, "end": v(-139.7, 3079.75) * mm});
            skLineSegment(sketch, "E6.45.3.3", {"start": v(-904.87, 2924.17) * mm, "end": v(-295.27, 2924.17) * mm});
            skLineSegment(sketch, "E6.0.3.4", {"start": v(-1517.65, 3384.55) * mm, "end": v(-908.05, 3384.55) * mm});
            skLineSegment(sketch, "E6.3.3.4", {"start": v(-1365.25, 3540.12) * mm, "end": v(-1517.65, 3540.12) * mm});
            skLineSegment(sketch, "E6.6.3.4", {"start": v(-1362.07, 3540.12) * mm, "end": v(-1362.07, 3692.52) * mm});
            skLineSegment(sketch, "E6.9.3.4", {"start": v(-1209.67, 3695.7) * mm, "end": v(-1362.07, 3695.7) * mm});
            skLineSegment(sketch, "E6.12.3.4", {"start": v(-1362.07, 3540.12) * mm, "end": v(-752.47, 3540.12) * mm});
            skLineSegment(sketch, "E6.15.3.4", {"start": v(-1365.25, 3540.12) * mm, "end": v(-1365.25, 4149.72) * mm});
            skLineSegment(sketch, "E6.18.3.4", {"start": v(-1362.07, 3692.52) * mm, "end": v(-752.47, 3692.52) * mm});
            skLineSegment(sketch, "E6.21.3.4", {"start": v(-1209.67, 4305.3) * mm, "end": v(-1362.07, 4305.3) * mm});
            skLineSegment(sketch, "E6.24.3.4", {"start": v(-1517.65, 3540.12) * mm, "end": v(-1517.65, 4149.72) * mm});
            skLineSegment(sketch, "E6.27.3.4", {"start": v(-1362.07, 3695.7) * mm, "end": v(-1362.07, 4305.3) * mm});
            skLineSegment(sketch, "E6.30.3.4", {"start": v(-908.05, 3384.55) * mm, "end": v(-908.05, 3536.95) * mm});
            skLineSegment(sketch, "E6.33.3.4", {"start": v(-1209.67, 3695.7) * mm, "end": v(-1209.67, 4305.3) * mm});
            skLineSegment(sketch, "E6.36.3.4", {"start": v(-1517.65, 3384.55) * mm, "end": v(-1517.65, 3536.95) * mm});
            skLineSegment(sketch, "E6.39.3.4", {"start": v(-1365.25, 4149.72) * mm, "end": v(-1517.65, 4149.72) * mm});
            skLineSegment(sketch, "E6.42.3.4", {"start": v(-752.47, 3540.12) * mm, "end": v(-752.47, 3692.52) * mm});
            skLineSegment(sketch, "E6.45.3.4", {"start": v(-1517.65, 3536.95) * mm, "end": v(-908.05, 3536.95) * mm});
            skLineSegment(sketch, "E6.0.4.2", {"start": v(19.05, 2470.15) * mm, "end": v(628.65, 2470.15) * mm});
            skLineSegment(sketch, "E6.3.4.2", {"start": v(171.45, 2625.72) * mm, "end": v(19.05, 2625.72) * mm});
            skLineSegment(sketch, "E6.6.4.2", {"start": v(174.63, 2625.72) * mm, "end": v(174.63, 2778.12) * mm});
            skLineSegment(sketch, "E6.9.4.2", {"start": v(327.03, 2781.3) * mm, "end": v(174.63, 2781.3) * mm});
            skLineSegment(sketch, "E6.12.4.2", {"start": v(174.63, 2625.72) * mm, "end": v(784.23, 2625.72) * mm});
            skLineSegment(sketch, "E6.15.4.2", {"start": v(171.45, 2625.72) * mm, "end": v(171.45, 3235.32) * mm});
            skLineSegment(sketch, "E6.18.4.2", {"start": v(174.63, 2778.12) * mm, "end": v(784.23, 2778.12) * mm});
            skLineSegment(sketch, "E6.21.4.2", {"start": v(327.03, 3390.9) * mm, "end": v(174.63, 3390.9) * mm});
            skLineSegment(sketch, "E6.24.4.2", {"start": v(19.05, 2625.72) * mm, "end": v(19.05, 3235.32) * mm});
            skLineSegment(sketch, "E6.27.4.2", {"start": v(174.63, 2781.3) * mm, "end": v(174.63, 3390.9) * mm});
            skLineSegment(sketch, "E6.30.4.2", {"start": v(628.65, 2470.15) * mm, "end": v(628.65, 2622.55) * mm});
            skLineSegment(sketch, "E6.33.4.2", {"start": v(327.03, 2781.3) * mm, "end": v(327.03, 3390.9) * mm});
            skLineSegment(sketch, "E6.36.4.2", {"start": v(19.05, 2470.15) * mm, "end": v(19.05, 2622.55) * mm});
            skLineSegment(sketch, "E6.39.4.2", {"start": v(171.45, 3235.32) * mm, "end": v(19.05, 3235.32) * mm});
            skLineSegment(sketch, "E6.42.4.2", {"start": v(784.23, 2625.72) * mm, "end": v(784.23, 2778.12) * mm});
            skLineSegment(sketch, "E6.45.4.2", {"start": v(19.05, 2622.55) * mm, "end": v(628.65, 2622.55) * mm});
            skLineSegment(sketch, "E6.0.4.3", {"start": v(-593.72, 3082.92) * mm, "end": v(15.88, 3082.92) * mm});
            skLineSegment(sketch, "E6.3.4.3", {"start": v(-441.32, 3238.5) * mm, "end": v(-593.72, 3238.5) * mm});
            skLineSegment(sketch, "E6.6.4.3", {"start": v(-438.15, 3238.5) * mm, "end": v(-438.15, 3390.9) * mm});
            skLineSegment(sketch, "E6.9.4.3", {"start": v(-285.75, 3394.07) * mm, "end": v(-438.15, 3394.07) * mm});
            skLineSegment(sketch, "E6.12.4.3", {"start": v(-438.15, 3238.5) * mm, "end": v(171.45, 3238.5) * mm});
            skLineSegment(sketch, "E6.15.4.3", {"start": v(-441.32, 3238.5) * mm, "end": v(-441.32, 3848.1) * mm});
            skLineSegment(sketch, "E6.18.4.3", {"start": v(-438.15, 3390.9) * mm, "end": v(171.45, 3390.9) * mm});
            skLineSegment(sketch, "E6.21.4.3", {"start": v(-285.75, 4003.67) * mm, "end": v(-438.15, 4003.67) * mm});
            skLineSegment(sketch, "E6.24.4.3", {"start": v(-593.72, 3238.5) * mm, "end": v(-593.72, 3848.1) * mm});
            skLineSegment(sketch, "E6.27.4.3", {"start": v(-438.15, 3394.07) * mm, "end": v(-438.15, 4003.67) * mm});
            skLineSegment(sketch, "E6.30.4.3", {"start": v(15.88, 3082.92) * mm, "end": v(15.88, 3235.32) * mm});
            skLineSegment(sketch, "E6.33.4.3", {"start": v(-285.75, 3394.07) * mm, "end": v(-285.75, 4003.67) * mm});
            skLineSegment(sketch, "E6.36.4.3", {"start": v(-593.72, 3082.92) * mm, "end": v(-593.72, 3235.32) * mm});
            skLineSegment(sketch, "E6.39.4.3", {"start": v(-441.32, 3848.1) * mm, "end": v(-593.72, 3848.1) * mm});
            skLineSegment(sketch, "E6.42.4.3", {"start": v(171.45, 3238.5) * mm, "end": v(171.45, 3390.9) * mm});
            skLineSegment(sketch, "E6.45.4.3", {"start": v(-593.72, 3235.32) * mm, "end": v(15.88, 3235.32) * mm});
            skLineSegment(sketch, "E6.0.4.4", {"start": v(-1206.5, 3695.7) * mm, "end": v(-596.9, 3695.7) * mm});
            skLineSegment(sketch, "E6.3.4.4", {"start": v(-1054.1, 3851.27) * mm, "end": v(-1206.5, 3851.27) * mm});
            skLineSegment(sketch, "E6.6.4.4", {"start": v(-1050.92, 3851.27) * mm, "end": v(-1050.92, 4003.67) * mm});
            skLineSegment(sketch, "E6.9.4.4", {"start": v(-898.52, 4006.85) * mm, "end": v(-1050.92, 4006.85) * mm});
            skLineSegment(sketch, "E6.12.4.4", {"start": v(-1050.92, 3851.27) * mm, "end": v(-441.32, 3851.27) * mm});
            skLineSegment(sketch, "E6.15.4.4", {"start": v(-1054.1, 3851.27) * mm, "end": v(-1054.1, 4460.87) * mm});
            skLineSegment(sketch, "E6.18.4.4", {"start": v(-1050.92, 4003.67) * mm, "end": v(-441.32, 4003.67) * mm});
            skLineSegment(sketch, "E6.21.4.4", {"start": v(-898.52, 4616.45) * mm, "end": v(-1050.92, 4616.45) * mm});
            skLineSegment(sketch, "E6.24.4.4", {"start": v(-1206.5, 3851.27) * mm, "end": v(-1206.5, 4460.87) * mm});
            skLineSegment(sketch, "E6.27.4.4", {"start": v(-1050.92, 4006.85) * mm, "end": v(-1050.92, 4616.45) * mm});
            skLineSegment(sketch, "E6.30.4.4", {"start": v(-596.9, 3695.7) * mm, "end": v(-596.9, 3848.1) * mm});
            skLineSegment(sketch, "E6.33.4.4", {"start": v(-898.52, 4006.85) * mm, "end": v(-898.52, 4616.45) * mm});
            skLineSegment(sketch, "E6.36.4.4", {"start": v(-1206.5, 3695.7) * mm, "end": v(-1206.5, 3848.1) * mm});
            skLineSegment(sketch, "E6.39.4.4", {"start": v(-1054.1, 4460.87) * mm, "end": v(-1206.5, 4460.87) * mm});
            skLineSegment(sketch, "E6.42.4.4", {"start": v(-441.32, 3851.27) * mm, "end": v(-441.32, 4003.67) * mm});
            skLineSegment(sketch, "E6.45.4.4", {"start": v(-1206.5, 3848.1) * mm, "end": v(-596.9, 3848.1) * mm});
            skLineSegment(sketch, "E6.0.5.2", {"start": v(330.2, 2781.3) * mm, "end": v(939.8, 2781.3) * mm});
            skLineSegment(sketch, "E6.3.5.2", {"start": v(482.6, 2936.87) * mm, "end": v(330.2, 2936.87) * mm});
            skLineSegment(sketch, "E6.6.5.2", {"start": v(485.78, 2936.87) * mm, "end": v(485.78, 3089.27) * mm});
            skLineSegment(sketch, "E6.9.5.2", {"start": v(638.18, 3092.45) * mm, "end": v(485.78, 3092.45) * mm});
            skLineSegment(sketch, "E6.12.5.2", {"start": v(485.78, 2936.87) * mm, "end": v(1095.38, 2936.87) * mm});
            skLineSegment(sketch, "E6.15.5.2", {"start": v(482.6, 2936.87) * mm, "end": v(482.6, 3546.47) * mm});
            skLineSegment(sketch, "E6.18.5.2", {"start": v(485.78, 3089.27) * mm, "end": v(1095.38, 3089.27) * mm});
            skLineSegment(sketch, "E6.21.5.2", {"start": v(638.18, 3702.05) * mm, "end": v(485.78, 3702.05) * mm});
            skLineSegment(sketch, "E6.24.5.2", {"start": v(330.2, 2936.87) * mm, "end": v(330.2, 3546.47) * mm});
            skLineSegment(sketch, "E6.27.5.2", {"start": v(485.78, 3092.45) * mm, "end": v(485.78, 3702.05) * mm});
            skLineSegment(sketch, "E6.30.5.2", {"start": v(939.8, 2781.3) * mm, "end": v(939.8, 2933.7) * mm});
            skLineSegment(sketch, "E6.33.5.2", {"start": v(638.18, 3092.45) * mm, "end": v(638.18, 3702.05) * mm});
            skLineSegment(sketch, "E6.36.5.2", {"start": v(330.2, 2781.3) * mm, "end": v(330.2, 2933.7) * mm});
            skLineSegment(sketch, "E6.39.5.2", {"start": v(482.6, 3546.47) * mm, "end": v(330.2, 3546.47) * mm});
            skLineSegment(sketch, "E6.42.5.2", {"start": v(1095.38, 2936.87) * mm, "end": v(1095.38, 3089.27) * mm});
            skLineSegment(sketch, "E6.45.5.2", {"start": v(330.2, 2933.7) * mm, "end": v(939.8, 2933.7) * mm});
            skLineSegment(sketch, "E6.0.5.3", {"start": v(-282.57, 3394.07) * mm, "end": v(327.03, 3394.07) * mm});
            skLineSegment(sketch, "E6.3.5.3", {"start": v(-130.17, 3549.65) * mm, "end": v(-282.57, 3549.65) * mm});
            skLineSegment(sketch, "E6.6.5.3", {"start": v(-127, 3549.65) * mm, "end": v(-127, 3702.05) * mm});
            skLineSegment(sketch, "E6.9.5.3", {"start": v(25.4, 3705.22) * mm, "end": v(-127, 3705.22) * mm});
            skLineSegment(sketch, "E6.12.5.3", {"start": v(-127, 3549.65) * mm, "end": v(482.6, 3549.65) * mm});
            skLineSegment(sketch, "E6.15.5.3", {"start": v(-130.17, 3549.65) * mm, "end": v(-130.17, 4159.25) * mm});
            skLineSegment(sketch, "E6.18.5.3", {"start": v(-127, 3702.05) * mm, "end": v(482.6, 3702.05) * mm});
            skLineSegment(sketch, "E6.21.5.3", {"start": v(25.4, 4314.82) * mm, "end": v(-127, 4314.82) * mm});
            skLineSegment(sketch, "E6.24.5.3", {"start": v(-282.57, 3549.65) * mm, "end": v(-282.57, 4159.25) * mm});
            skLineSegment(sketch, "E6.27.5.3", {"start": v(-127, 3705.22) * mm, "end": v(-127, 4314.82) * mm});
            skLineSegment(sketch, "E6.30.5.3", {"start": v(327.03, 3394.07) * mm, "end": v(327.03, 3546.47) * mm});
            skLineSegment(sketch, "E6.33.5.3", {"start": v(25.4, 3705.22) * mm, "end": v(25.4, 4314.82) * mm});
            skLineSegment(sketch, "E6.36.5.3", {"start": v(-282.57, 3394.07) * mm, "end": v(-282.57, 3546.47) * mm});
            skLineSegment(sketch, "E6.39.5.3", {"start": v(-130.17, 4159.25) * mm, "end": v(-282.57, 4159.25) * mm});
            skLineSegment(sketch, "E6.42.5.3", {"start": v(482.6, 3549.65) * mm, "end": v(482.6, 3702.05) * mm});
            skLineSegment(sketch, "E6.45.5.3", {"start": v(-282.57, 3546.47) * mm, "end": v(327.03, 3546.47) * mm});
            skLineSegment(sketch, "E6.0.5.4", {"start": v(-895.35, 4006.85) * mm, "end": v(-285.75, 4006.85) * mm});
            skLineSegment(sketch, "E6.3.5.4", {"start": v(-742.95, 4162.42) * mm, "end": v(-895.35, 4162.42) * mm});
            skLineSegment(sketch, "E6.6.5.4", {"start": v(-739.77, 4162.42) * mm, "end": v(-739.77, 4314.82) * mm});
            skLineSegment(sketch, "E6.9.5.4", {"start": v(-587.37, 4318) * mm, "end": v(-739.77, 4318) * mm});
            skLineSegment(sketch, "E6.12.5.4", {"start": v(-739.77, 4162.42) * mm, "end": v(-130.17, 4162.42) * mm});
            skLineSegment(sketch, "E6.15.5.4", {"start": v(-742.95, 4162.42) * mm, "end": v(-742.95, 4772.02) * mm});
            skLineSegment(sketch, "E6.18.5.4", {"start": v(-739.77, 4314.82) * mm, "end": v(-130.17, 4314.82) * mm});
            skLineSegment(sketch, "E6.21.5.4", {"start": v(-587.37, 4927.6) * mm, "end": v(-739.77, 4927.6) * mm});
            skLineSegment(sketch, "E6.24.5.4", {"start": v(-895.35, 4162.42) * mm, "end": v(-895.35, 4772.02) * mm});
            skLineSegment(sketch, "E6.27.5.4", {"start": v(-739.77, 4318) * mm, "end": v(-739.77, 4927.6) * mm});
            skLineSegment(sketch, "E6.30.5.4", {"start": v(-285.75, 4006.85) * mm, "end": v(-285.75, 4159.25) * mm});
            skLineSegment(sketch, "E6.33.5.4", {"start": v(-587.37, 4318) * mm, "end": v(-587.37, 4927.6) * mm});
            skLineSegment(sketch, "E6.36.5.4", {"start": v(-895.35, 4006.85) * mm, "end": v(-895.35, 4159.25) * mm});
            skLineSegment(sketch, "E6.39.5.4", {"start": v(-742.95, 4772.02) * mm, "end": v(-895.35, 4772.02) * mm});
            skLineSegment(sketch, "E6.42.5.4", {"start": v(-130.17, 4162.42) * mm, "end": v(-130.17, 4314.82) * mm});
            skLineSegment(sketch, "E6.45.5.4", {"start": v(-895.35, 4159.25) * mm, "end": v(-285.75, 4159.25) * mm});
            skLineSegment(sketch, "E7.0.6.0", {"start": v(1866.9, 1866.9) * mm, "end": v(2476.5, 1866.9) * mm});
            skLineSegment(sketch, "E7.3.6.0", {"start": v(2019.3, 2022.47) * mm, "end": v(1866.9, 2022.47) * mm});
            skLineSegment(sketch, "E7.6.6.0", {"start": v(2022.48, 2022.47) * mm, "end": v(2022.48, 2174.87) * mm});
            skLineSegment(sketch, "E7.9.6.0", {"start": v(2174.88, 2178.05) * mm, "end": v(2022.48, 2178.05) * mm});
            skLineSegment(sketch, "E7.12.6.0", {"start": v(2022.48, 2022.47) * mm, "end": v(2632.08, 2022.47) * mm});
            skLineSegment(sketch, "E7.15.6.0", {"start": v(2019.3, 2022.47) * mm, "end": v(2019.3, 2632.07) * mm});
            skLineSegment(sketch, "E7.18.6.0", {"start": v(2022.48, 2174.87) * mm, "end": v(2632.08, 2174.87) * mm});
            skLineSegment(sketch, "E7.21.6.0", {"start": v(2174.88, 2787.65) * mm, "end": v(2022.48, 2787.65) * mm});
            skLineSegment(sketch, "E7.24.6.0", {"start": v(1866.9, 2022.47) * mm, "end": v(1866.9, 2632.07) * mm});
            skLineSegment(sketch, "E7.27.6.0", {"start": v(2022.48, 2178.05) * mm, "end": v(2022.48, 2787.65) * mm});
            skLineSegment(sketch, "E7.30.6.0", {"start": v(2476.5, 1866.9) * mm, "end": v(2476.5, 2019.3) * mm});
            skLineSegment(sketch, "E7.33.6.0", {"start": v(2174.88, 2178.05) * mm, "end": v(2174.88, 2787.65) * mm});
            skLineSegment(sketch, "E7.36.6.0", {"start": v(1866.9, 1866.9) * mm, "end": v(1866.9, 2019.3) * mm});
            skLineSegment(sketch, "E7.39.6.0", {"start": v(2019.3, 2632.07) * mm, "end": v(1866.9, 2632.07) * mm});
            skLineSegment(sketch, "E7.42.6.0", {"start": v(2632.08, 2022.47) * mm, "end": v(2632.08, 2174.87) * mm});
            skLineSegment(sketch, "E7.45.6.0", {"start": v(1866.9, 2019.3) * mm, "end": v(2476.5, 2019.3) * mm});
            skLineSegment(sketch, "E7.0.6.1", {"start": v(1254.13, 2479.67) * mm, "end": v(1863.73, 2479.67) * mm});
            skLineSegment(sketch, "E7.3.6.1", {"start": v(1406.53, 2635.25) * mm, "end": v(1254.13, 2635.25) * mm});
            skLineSegment(sketch, "E7.6.6.1", {"start": v(1409.7, 2635.25) * mm, "end": v(1409.7, 2787.65) * mm});
            skLineSegment(sketch, "E7.9.6.1", {"start": v(1562.1, 2790.82) * mm, "end": v(1409.7, 2790.82) * mm});
            skLineSegment(sketch, "E7.12.6.1", {"start": v(1409.7, 2635.25) * mm, "end": v(2019.3, 2635.25) * mm});
            skLineSegment(sketch, "E7.15.6.1", {"start": v(1406.53, 2635.25) * mm, "end": v(1406.53, 3244.85) * mm});
            skLineSegment(sketch, "E7.18.6.1", {"start": v(1409.7, 2787.65) * mm, "end": v(2019.3, 2787.65) * mm});
            skLineSegment(sketch, "E7.21.6.1", {"start": v(1562.1, 3400.42) * mm, "end": v(1409.7, 3400.42) * mm});
            skLineSegment(sketch, "E7.24.6.1", {"start": v(1254.13, 2635.25) * mm, "end": v(1254.13, 3244.85) * mm});
            skLineSegment(sketch, "E7.27.6.1", {"start": v(1409.7, 2790.82) * mm, "end": v(1409.7, 3400.42) * mm});
            skLineSegment(sketch, "E7.30.6.1", {"start": v(1863.73, 2479.67) * mm, "end": v(1863.73, 2632.07) * mm});
            skLineSegment(sketch, "E7.33.6.1", {"start": v(1562.1, 2790.82) * mm, "end": v(1562.1, 3400.42) * mm});
            skLineSegment(sketch, "E7.36.6.1", {"start": v(1254.13, 2479.67) * mm, "end": v(1254.13, 2632.07) * mm});
            skLineSegment(sketch, "E7.39.6.1", {"start": v(1406.53, 3244.85) * mm, "end": v(1254.13, 3244.85) * mm});
            skLineSegment(sketch, "E7.42.6.1", {"start": v(2019.3, 2635.25) * mm, "end": v(2019.3, 2787.65) * mm});
            skLineSegment(sketch, "E7.45.6.1", {"start": v(1254.13, 2632.07) * mm, "end": v(1863.73, 2632.07) * mm});
            skLineSegment(sketch, "E7.0.6.2", {"start": v(641.35, 3092.45) * mm, "end": v(1250.95, 3092.45) * mm});
            skLineSegment(sketch, "E7.3.6.2", {"start": v(793.75, 3248.02) * mm, "end": v(641.35, 3248.02) * mm});
            skLineSegment(sketch, "E7.6.6.2", {"start": v(796.92, 3248.02) * mm, "end": v(796.92, 3400.42) * mm});
            skLineSegment(sketch, "E7.9.6.2", {"start": v(949.32, 3403.6) * mm, "end": v(796.92, 3403.6) * mm});
            skLineSegment(sketch, "E7.12.6.2", {"start": v(796.92, 3248.02) * mm, "end": v(1406.52, 3248.02) * mm});
            skLineSegment(sketch, "E7.15.6.2", {"start": v(793.75, 3248.02) * mm, "end": v(793.75, 3857.62) * mm});
            skLineSegment(sketch, "E7.18.6.2", {"start": v(796.92, 3400.42) * mm, "end": v(1406.52, 3400.42) * mm});
            skLineSegment(sketch, "E7.21.6.2", {"start": v(949.32, 4013.2) * mm, "end": v(796.92, 4013.2) * mm});
            skLineSegment(sketch, "E7.24.6.2", {"start": v(641.35, 3248.02) * mm, "end": v(641.35, 3857.62) * mm});
            skLineSegment(sketch, "E7.27.6.2", {"start": v(796.92, 3403.6) * mm, "end": v(796.92, 4013.2) * mm});
            skLineSegment(sketch, "E7.30.6.2", {"start": v(1250.95, 3092.45) * mm, "end": v(1250.95, 3244.85) * mm});
            skLineSegment(sketch, "E7.33.6.2", {"start": v(949.32, 3403.6) * mm, "end": v(949.32, 4013.2) * mm});
            skLineSegment(sketch, "E7.36.6.2", {"start": v(641.35, 3092.45) * mm, "end": v(641.35, 3244.85) * mm});
            skLineSegment(sketch, "E7.39.6.2", {"start": v(793.75, 3857.62) * mm, "end": v(641.35, 3857.62) * mm});
            skLineSegment(sketch, "E7.42.6.2", {"start": v(1406.52, 3248.02) * mm, "end": v(1406.52, 3400.42) * mm});
            skLineSegment(sketch, "E7.45.6.2", {"start": v(641.35, 3244.85) * mm, "end": v(1250.95, 3244.85) * mm});
            skLineSegment(sketch, "E7.0.6.3", {"start": v(28.57, 3705.22) * mm, "end": v(638.17, 3705.22) * mm});
            skLineSegment(sketch, "E7.3.6.3", {"start": v(180.97, 3860.8) * mm, "end": v(28.57, 3860.8) * mm});
            skLineSegment(sketch, "E7.6.6.3", {"start": v(184.15, 3860.8) * mm, "end": v(184.15, 4013.2) * mm});
            skLineSegment(sketch, "E7.9.6.3", {"start": v(336.55, 4016.37) * mm, "end": v(184.15, 4016.37) * mm});
            skLineSegment(sketch, "E7.12.6.3", {"start": v(184.15, 3860.8) * mm, "end": v(793.75, 3860.8) * mm});
            skLineSegment(sketch, "E7.15.6.3", {"start": v(180.97, 3860.8) * mm, "end": v(180.97, 4470.4) * mm});
            skLineSegment(sketch, "E7.18.6.3", {"start": v(184.15, 4013.2) * mm, "end": v(793.75, 4013.2) * mm});
            skLineSegment(sketch, "E7.21.6.3", {"start": v(336.55, 4625.97) * mm, "end": v(184.15, 4625.97) * mm});
            skLineSegment(sketch, "E7.24.6.3", {"start": v(28.57, 3860.8) * mm, "end": v(28.57, 4470.4) * mm});
            skLineSegment(sketch, "E7.27.6.3", {"start": v(184.15, 4016.37) * mm, "end": v(184.15, 4625.97) * mm});
            skLineSegment(sketch, "E7.30.6.3", {"start": v(638.17, 3705.22) * mm, "end": v(638.17, 3857.62) * mm});
            skLineSegment(sketch, "E7.33.6.3", {"start": v(336.55, 4016.37) * mm, "end": v(336.55, 4625.97) * mm});
            skLineSegment(sketch, "E7.36.6.3", {"start": v(28.57, 3705.22) * mm, "end": v(28.57, 3857.62) * mm});
            skLineSegment(sketch, "E7.39.6.3", {"start": v(180.97, 4470.4) * mm, "end": v(28.57, 4470.4) * mm});
            skLineSegment(sketch, "E7.42.6.3", {"start": v(793.75, 3860.8) * mm, "end": v(793.75, 4013.2) * mm});
            skLineSegment(sketch, "E7.45.6.3", {"start": v(28.57, 3857.62) * mm, "end": v(638.17, 3857.62) * mm});
            skLineSegment(sketch, "E7.0.6.4", {"start": v(-584.2, 4318) * mm, "end": v(25.4, 4318) * mm});
            skLineSegment(sketch, "E7.3.6.4", {"start": v(-431.8, 4473.57) * mm, "end": v(-584.2, 4473.57) * mm});
            skLineSegment(sketch, "E7.6.6.4", {"start": v(-428.63, 4473.57) * mm, "end": v(-428.63, 4625.97) * mm});
            skLineSegment(sketch, "E7.9.6.4", {"start": v(-276.23, 4629.15) * mm, "end": v(-428.63, 4629.15) * mm});
            skLineSegment(sketch, "E7.12.6.4", {"start": v(-428.63, 4473.57) * mm, "end": v(180.97, 4473.57) * mm});
            skLineSegment(sketch, "E7.15.6.4", {"start": v(-431.8, 4473.57) * mm, "end": v(-431.8, 5083.18) * mm});
            skLineSegment(sketch, "E7.18.6.4", {"start": v(-428.63, 4625.97) * mm, "end": v(180.97, 4625.97) * mm});
            skLineSegment(sketch, "E7.21.6.4", {"start": v(-276.23, 5238.75) * mm, "end": v(-428.63, 5238.75) * mm});
            skLineSegment(sketch, "E7.24.6.4", {"start": v(-584.2, 4473.57) * mm, "end": v(-584.2, 5083.18) * mm});
            skLineSegment(sketch, "E7.27.6.4", {"start": v(-428.63, 4629.15) * mm, "end": v(-428.63, 5238.75) * mm});
            skLineSegment(sketch, "E7.30.6.4", {"start": v(25.4, 4318) * mm, "end": v(25.4, 4470.4) * mm});
            skLineSegment(sketch, "E7.33.6.4", {"start": v(-276.23, 4629.15) * mm, "end": v(-276.23, 5238.75) * mm});
            skLineSegment(sketch, "E7.36.6.4", {"start": v(-584.2, 4318) * mm, "end": v(-584.2, 4470.4) * mm});
            skLineSegment(sketch, "E7.39.6.4", {"start": v(-431.8, 5083.18) * mm, "end": v(-584.2, 5083.18) * mm});
            skLineSegment(sketch, "E7.42.6.4", {"start": v(180.97, 4473.57) * mm, "end": v(180.97, 4625.97) * mm});
            skLineSegment(sketch, "E7.45.6.4", {"start": v(-584.2, 4470.4) * mm, "end": v(25.4, 4470.4) * mm});
            skLineSegment(sketch, "E7.0.7.0", {"start": v(2178.05, 2178.05) * mm, "end": v(2787.65, 2178.05) * mm});
            skLineSegment(sketch, "E7.3.7.0", {"start": v(2330.45, 2333.62) * mm, "end": v(2178.05, 2333.62) * mm});
            skLineSegment(sketch, "E7.6.7.0", {"start": v(2333.63, 2333.62) * mm, "end": v(2333.63, 2486.02) * mm});
            skLineSegment(sketch, "E7.9.7.0", {"start": v(2486.03, 2489.2) * mm, "end": v(2333.63, 2489.2) * mm});
            skLineSegment(sketch, "E7.12.7.0", {"start": v(2333.63, 2333.62) * mm, "end": v(2943.23, 2333.62) * mm});
            skLineSegment(sketch, "E7.15.7.0", {"start": v(2330.45, 2333.62) * mm, "end": v(2330.45, 2943.22) * mm});
            skLineSegment(sketch, "E7.18.7.0", {"start": v(2333.63, 2486.02) * mm, "end": v(2943.23, 2486.02) * mm});
            skLineSegment(sketch, "E7.21.7.0", {"start": v(2486.03, 3098.8) * mm, "end": v(2333.63, 3098.8) * mm});
            skLineSegment(sketch, "E7.24.7.0", {"start": v(2178.05, 2333.62) * mm, "end": v(2178.05, 2943.22) * mm});
            skLineSegment(sketch, "E7.27.7.0", {"start": v(2333.63, 2489.2) * mm, "end": v(2333.63, 3098.8) * mm});
            skLineSegment(sketch, "E7.30.7.0", {"start": v(2787.65, 2178.05) * mm, "end": v(2787.65, 2330.45) * mm});
            skLineSegment(sketch, "E7.33.7.0", {"start": v(2486.03, 2489.2) * mm, "end": v(2486.03, 3098.8) * mm});
            skLineSegment(sketch, "E7.36.7.0", {"start": v(2178.05, 2178.05) * mm, "end": v(2178.05, 2330.45) * mm});
            skLineSegment(sketch, "E7.39.7.0", {"start": v(2330.45, 2943.22) * mm, "end": v(2178.05, 2943.22) * mm});
            skLineSegment(sketch, "E7.42.7.0", {"start": v(2943.23, 2333.62) * mm, "end": v(2943.23, 2486.02) * mm});
            skLineSegment(sketch, "E7.45.7.0", {"start": v(2178.05, 2330.45) * mm, "end": v(2787.65, 2330.45) * mm});
            skLineSegment(sketch, "E7.0.7.1", {"start": v(1565.28, 2790.82) * mm, "end": v(2174.88, 2790.82) * mm});
            skLineSegment(sketch, "E7.3.7.1", {"start": v(1717.68, 2946.4) * mm, "end": v(1565.28, 2946.4) * mm});
            skLineSegment(sketch, "E7.6.7.1", {"start": v(1720.85, 2946.4) * mm, "end": v(1720.85, 3098.8) * mm});
            skLineSegment(sketch, "E7.9.7.1", {"start": v(1873.25, 3101.97) * mm, "end": v(1720.85, 3101.97) * mm});
            skLineSegment(sketch, "E7.12.7.1", {"start": v(1720.85, 2946.4) * mm, "end": v(2330.45, 2946.4) * mm});
            skLineSegment(sketch, "E7.15.7.1", {"start": v(1717.68, 2946.4) * mm, "end": v(1717.68, 3556) * mm});
            skLineSegment(sketch, "E7.18.7.1", {"start": v(1720.85, 3098.8) * mm, "end": v(2330.45, 3098.8) * mm});
            skLineSegment(sketch, "E7.21.7.1", {"start": v(1873.25, 3711.57) * mm, "end": v(1720.85, 3711.57) * mm});
            skLineSegment(sketch, "E7.24.7.1", {"start": v(1565.28, 2946.4) * mm, "end": v(1565.28, 3556) * mm});
            skLineSegment(sketch, "E7.27.7.1", {"start": v(1720.85, 3101.97) * mm, "end": v(1720.85, 3711.57) * mm});
            skLineSegment(sketch, "E7.30.7.1", {"start": v(2174.88, 2790.82) * mm, "end": v(2174.88, 2943.22) * mm});
            skLineSegment(sketch, "E7.33.7.1", {"start": v(1873.25, 3101.97) * mm, "end": v(1873.25, 3711.57) * mm});
            skLineSegment(sketch, "E7.36.7.1", {"start": v(1565.28, 2790.82) * mm, "end": v(1565.28, 2943.22) * mm});
            skLineSegment(sketch, "E7.39.7.1", {"start": v(1717.68, 3556) * mm, "end": v(1565.28, 3556) * mm});
            skLineSegment(sketch, "E7.42.7.1", {"start": v(2330.45, 2946.4) * mm, "end": v(2330.45, 3098.8) * mm});
            skLineSegment(sketch, "E7.45.7.1", {"start": v(1565.28, 2943.22) * mm, "end": v(2174.88, 2943.22) * mm});
            skLineSegment(sketch, "E7.0.7.2", {"start": v(952.5, 3403.6) * mm, "end": v(1562.1, 3403.6) * mm});
            skLineSegment(sketch, "E7.3.7.2", {"start": v(1104.9, 3559.17) * mm, "end": v(952.5, 3559.17) * mm});
            skLineSegment(sketch, "E7.6.7.2", {"start": v(1108.07, 3559.17) * mm, "end": v(1108.07, 3711.57) * mm});
            skLineSegment(sketch, "E7.9.7.2", {"start": v(1260.47, 3714.75) * mm, "end": v(1108.07, 3714.75) * mm});
            skLineSegment(sketch, "E7.12.7.2", {"start": v(1108.07, 3559.17) * mm, "end": v(1717.67, 3559.17) * mm});
            skLineSegment(sketch, "E7.15.7.2", {"start": v(1104.9, 3559.17) * mm, "end": v(1104.9, 4168.77) * mm});
            skLineSegment(sketch, "E7.18.7.2", {"start": v(1108.07, 3711.57) * mm, "end": v(1717.67, 3711.57) * mm});
            skLineSegment(sketch, "E7.21.7.2", {"start": v(1260.47, 4324.35) * mm, "end": v(1108.07, 4324.35) * mm});
            skLineSegment(sketch, "E7.24.7.2", {"start": v(952.5, 3559.17) * mm, "end": v(952.5, 4168.77) * mm});
            skLineSegment(sketch, "E7.27.7.2", {"start": v(1108.07, 3714.75) * mm, "end": v(1108.07, 4324.35) * mm});
            skLineSegment(sketch, "E7.30.7.2", {"start": v(1562.1, 3403.6) * mm, "end": v(1562.1, 3556) * mm});
            skLineSegment(sketch, "E7.33.7.2", {"start": v(1260.47, 3714.75) * mm, "end": v(1260.47, 4324.35) * mm});
            skLineSegment(sketch, "E7.36.7.2", {"start": v(952.5, 3403.6) * mm, "end": v(952.5, 3556) * mm});
            skLineSegment(sketch, "E7.39.7.2", {"start": v(1104.9, 4168.77) * mm, "end": v(952.5, 4168.77) * mm});
            skLineSegment(sketch, "E7.42.7.2", {"start": v(1717.67, 3559.17) * mm, "end": v(1717.67, 3711.57) * mm});
            skLineSegment(sketch, "E7.45.7.2", {"start": v(952.5, 3556) * mm, "end": v(1562.1, 3556) * mm});
            skLineSegment(sketch, "E7.0.7.3", {"start": v(339.72, 4016.38) * mm, "end": v(949.32, 4016.38) * mm});
            skLineSegment(sketch, "E7.3.7.3", {"start": v(492.12, 4171.95) * mm, "end": v(339.72, 4171.95) * mm});
            skLineSegment(sketch, "E7.6.7.3", {"start": v(495.3, 4171.95) * mm, "end": v(495.3, 4324.35) * mm});
            skLineSegment(sketch, "E7.9.7.3", {"start": v(647.7, 4327.52) * mm, "end": v(495.3, 4327.52) * mm});
            skLineSegment(sketch, "E7.12.7.3", {"start": v(495.3, 4171.95) * mm, "end": v(1104.9, 4171.95) * mm});
            skLineSegment(sketch, "E7.15.7.3", {"start": v(492.12, 4171.95) * mm, "end": v(492.12, 4781.55) * mm});
            skLineSegment(sketch, "E7.18.7.3", {"start": v(495.3, 4324.35) * mm, "end": v(1104.9, 4324.35) * mm});
            skLineSegment(sketch, "E7.21.7.3", {"start": v(647.7, 4937.12) * mm, "end": v(495.3, 4937.12) * mm});
            skLineSegment(sketch, "E7.24.7.3", {"start": v(339.72, 4171.95) * mm, "end": v(339.72, 4781.55) * mm});
            skLineSegment(sketch, "E7.27.7.3", {"start": v(495.3, 4327.52) * mm, "end": v(495.3, 4937.12) * mm});
            skLineSegment(sketch, "E7.30.7.3", {"start": v(949.32, 4016.38) * mm, "end": v(949.32, 4168.78) * mm});
            skLineSegment(sketch, "E7.33.7.3", {"start": v(647.7, 4327.52) * mm, "end": v(647.7, 4937.12) * mm});
            skLineSegment(sketch, "E7.36.7.3", {"start": v(339.72, 4016.38) * mm, "end": v(339.72, 4168.78) * mm});
            skLineSegment(sketch, "E7.39.7.3", {"start": v(492.12, 4781.55) * mm, "end": v(339.72, 4781.55) * mm});
            skLineSegment(sketch, "E7.42.7.3", {"start": v(1104.9, 4171.95) * mm, "end": v(1104.9, 4324.35) * mm});
            skLineSegment(sketch, "E7.45.7.3", {"start": v(339.72, 4168.78) * mm, "end": v(949.32, 4168.78) * mm});
            skLineSegment(sketch, "E7.0.7.4", {"start": v(-273.05, 4629.15) * mm, "end": v(336.55, 4629.15) * mm});
            skLineSegment(sketch, "E7.3.7.4", {"start": v(-120.65, 4784.72) * mm, "end": v(-273.05, 4784.72) * mm});
            skLineSegment(sketch, "E7.6.7.4", {"start": v(-117.48, 4784.72) * mm, "end": v(-117.48, 4937.12) * mm});
            skLineSegment(sketch, "E7.9.7.4", {"start": v(34.92, 4940.3) * mm, "end": v(-117.48, 4940.3) * mm});
            skLineSegment(sketch, "E7.12.7.4", {"start": v(-117.48, 4784.72) * mm, "end": v(492.12, 4784.72) * mm});
            skLineSegment(sketch, "E7.15.7.4", {"start": v(-120.65, 4784.72) * mm, "end": v(-120.65, 5394.32) * mm});
            skLineSegment(sketch, "E7.18.7.4", {"start": v(-117.48, 4937.12) * mm, "end": v(492.12, 4937.12) * mm});
            skLineSegment(sketch, "E7.21.7.4", {"start": v(34.92, 5549.9) * mm, "end": v(-117.48, 5549.9) * mm});
            skLineSegment(sketch, "E7.24.7.4", {"start": v(-273.05, 4784.72) * mm, "end": v(-273.05, 5394.32) * mm});
            skLineSegment(sketch, "E7.27.7.4", {"start": v(-117.48, 4940.3) * mm, "end": v(-117.48, 5549.9) * mm});
            skLineSegment(sketch, "E7.30.7.4", {"start": v(336.55, 4629.15) * mm, "end": v(336.55, 4781.55) * mm});
            skLineSegment(sketch, "E7.33.7.4", {"start": v(34.92, 4940.3) * mm, "end": v(34.92, 5549.9) * mm});
            skLineSegment(sketch, "E7.36.7.4", {"start": v(-273.05, 4629.15) * mm, "end": v(-273.05, 4781.55) * mm});
            skLineSegment(sketch, "E7.39.7.4", {"start": v(-120.65, 5394.32) * mm, "end": v(-273.05, 5394.32) * mm});
            skLineSegment(sketch, "E7.42.7.4", {"start": v(492.12, 4784.72) * mm, "end": v(492.12, 4937.12) * mm});
            skLineSegment(sketch, "E7.45.7.4", {"start": v(-273.05, 4781.55) * mm, "end": v(336.55, 4781.55) * mm});
            skLineSegment(sketch, "E8.0.8.0", {"start": v(2489.2, 2489.2) * mm, "end": v(3098.8, 2489.2) * mm});
            skLineSegment(sketch, "E8.3.8.0", {"start": v(2641.6, 2644.77) * mm, "end": v(2489.2, 2644.77) * mm});
            skLineSegment(sketch, "E8.6.8.0", {"start": v(2644.78, 2644.77) * mm, "end": v(2644.78, 2797.17) * mm});
            skLineSegment(sketch, "E8.9.8.0", {"start": v(2797.18, 2800.35) * mm, "end": v(2644.78, 2800.35) * mm});
            skLineSegment(sketch, "E8.12.8.0", {"start": v(2644.78, 2644.77) * mm, "end": v(3254.38, 2644.77) * mm});
            skLineSegment(sketch, "E8.15.8.0", {"start": v(2641.6, 2644.77) * mm, "end": v(2641.6, 3254.37) * mm});
            skLineSegment(sketch, "E8.18.8.0", {"start": v(2644.78, 2797.17) * mm, "end": v(3254.38, 2797.17) * mm});
            skLineSegment(sketch, "E8.21.8.0", {"start": v(2797.18, 3409.95) * mm, "end": v(2644.78, 3409.95) * mm});
            skLineSegment(sketch, "E8.24.8.0", {"start": v(2489.2, 2644.77) * mm, "end": v(2489.2, 3254.37) * mm});
            skLineSegment(sketch, "E8.27.8.0", {"start": v(2644.78, 2800.35) * mm, "end": v(2644.78, 3409.95) * mm});
            skLineSegment(sketch, "E8.30.8.0", {"start": v(3098.8, 2489.2) * mm, "end": v(3098.8, 2641.6) * mm});
            skLineSegment(sketch, "E8.33.8.0", {"start": v(2797.18, 2800.35) * mm, "end": v(2797.18, 3409.95) * mm});
            skLineSegment(sketch, "E8.36.8.0", {"start": v(2489.2, 2489.2) * mm, "end": v(2489.2, 2641.6) * mm});
            skLineSegment(sketch, "E8.39.8.0", {"start": v(2641.6, 3254.37) * mm, "end": v(2489.2, 3254.37) * mm});
            skLineSegment(sketch, "E8.42.8.0", {"start": v(3254.38, 2644.77) * mm, "end": v(3254.38, 2797.17) * mm});
            skLineSegment(sketch, "E8.45.8.0", {"start": v(2489.2, 2641.6) * mm, "end": v(3098.8, 2641.6) * mm});
            skLineSegment(sketch, "E8.0.8.1", {"start": v(1876.43, 3101.97) * mm, "end": v(2486.03, 3101.97) * mm});
            skLineSegment(sketch, "E8.3.8.1", {"start": v(2028.83, 3257.55) * mm, "end": v(1876.43, 3257.55) * mm});
            skLineSegment(sketch, "E8.6.8.1", {"start": v(2032, 3257.55) * mm, "end": v(2032, 3409.95) * mm});
            skLineSegment(sketch, "E8.9.8.1", {"start": v(2184.4, 3413.12) * mm, "end": v(2032, 3413.12) * mm});
            skLineSegment(sketch, "E8.12.8.1", {"start": v(2032, 3257.55) * mm, "end": v(2641.6, 3257.55) * mm});
            skLineSegment(sketch, "E8.15.8.1", {"start": v(2028.83, 3257.55) * mm, "end": v(2028.83, 3867.15) * mm});
            skLineSegment(sketch, "E8.18.8.1", {"start": v(2032, 3409.95) * mm, "end": v(2641.6, 3409.95) * mm});
            skLineSegment(sketch, "E8.21.8.1", {"start": v(2184.4, 4022.72) * mm, "end": v(2032, 4022.72) * mm});
            skLineSegment(sketch, "E8.24.8.1", {"start": v(1876.43, 3257.55) * mm, "end": v(1876.43, 3867.15) * mm});
            skLineSegment(sketch, "E8.27.8.1", {"start": v(2032, 3413.12) * mm, "end": v(2032, 4022.72) * mm});
            skLineSegment(sketch, "E8.30.8.1", {"start": v(2486.03, 3101.97) * mm, "end": v(2486.03, 3254.37) * mm});
            skLineSegment(sketch, "E8.33.8.1", {"start": v(2184.4, 3413.12) * mm, "end": v(2184.4, 4022.72) * mm});
            skLineSegment(sketch, "E8.36.8.1", {"start": v(1876.43, 3101.97) * mm, "end": v(1876.43, 3254.37) * mm});
            skLineSegment(sketch, "E8.39.8.1", {"start": v(2028.83, 3867.15) * mm, "end": v(1876.43, 3867.15) * mm});
            skLineSegment(sketch, "E8.42.8.1", {"start": v(2641.6, 3257.55) * mm, "end": v(2641.6, 3409.95) * mm});
            skLineSegment(sketch, "E8.45.8.1", {"start": v(1876.43, 3254.37) * mm, "end": v(2486.03, 3254.37) * mm});
            skLineSegment(sketch, "E8.0.8.2", {"start": v(1263.65, 3714.75) * mm, "end": v(1873.25, 3714.75) * mm});
            skLineSegment(sketch, "E8.3.8.2", {"start": v(1416.05, 3870.32) * mm, "end": v(1263.65, 3870.32) * mm});
            skLineSegment(sketch, "E8.6.8.2", {"start": v(1419.22, 3870.32) * mm, "end": v(1419.22, 4022.72) * mm});
            skLineSegment(sketch, "E8.9.8.2", {"start": v(1571.62, 4025.9) * mm, "end": v(1419.22, 4025.9) * mm});
            skLineSegment(sketch, "E8.12.8.2", {"start": v(1419.22, 3870.32) * mm, "end": v(2028.82, 3870.32) * mm});
            skLineSegment(sketch, "E8.15.8.2", {"start": v(1416.05, 3870.32) * mm, "end": v(1416.05, 4479.92) * mm});
            skLineSegment(sketch, "E8.18.8.2", {"start": v(1419.22, 4022.72) * mm, "end": v(2028.82, 4022.72) * mm});
            skLineSegment(sketch, "E8.21.8.2", {"start": v(1571.62, 4635.5) * mm, "end": v(1419.22, 4635.5) * mm});
            skLineSegment(sketch, "E8.24.8.2", {"start": v(1263.65, 3870.32) * mm, "end": v(1263.65, 4479.92) * mm});
            skLineSegment(sketch, "E8.27.8.2", {"start": v(1419.22, 4025.9) * mm, "end": v(1419.22, 4635.5) * mm});
            skLineSegment(sketch, "E8.30.8.2", {"start": v(1873.25, 3714.75) * mm, "end": v(1873.25, 3867.15) * mm});
            skLineSegment(sketch, "E8.33.8.2", {"start": v(1571.62, 4025.9) * mm, "end": v(1571.62, 4635.5) * mm});
            skLineSegment(sketch, "E8.36.8.2", {"start": v(1263.65, 3714.75) * mm, "end": v(1263.65, 3867.15) * mm});
            skLineSegment(sketch, "E8.39.8.2", {"start": v(1416.05, 4479.92) * mm, "end": v(1263.65, 4479.92) * mm});
            skLineSegment(sketch, "E8.42.8.2", {"start": v(2028.82, 3870.32) * mm, "end": v(2028.82, 4022.72) * mm});
            skLineSegment(sketch, "E8.45.8.2", {"start": v(1263.65, 3867.15) * mm, "end": v(1873.25, 3867.15) * mm});
            skLineSegment(sketch, "E8.0.8.3", {"start": v(650.87, 4327.52) * mm, "end": v(1260.47, 4327.52) * mm});
            skLineSegment(sketch, "E8.3.8.3", {"start": v(803.27, 4483.1) * mm, "end": v(650.87, 4483.1) * mm});
            skLineSegment(sketch, "E8.6.8.3", {"start": v(806.45, 4483.1) * mm, "end": v(806.45, 4635.5) * mm});
            skLineSegment(sketch, "E8.9.8.3", {"start": v(958.85, 4638.67) * mm, "end": v(806.45, 4638.67) * mm});
            skLineSegment(sketch, "E8.12.8.3", {"start": v(806.45, 4483.1) * mm, "end": v(1416.05, 4483.1) * mm});
            skLineSegment(sketch, "E8.15.8.3", {"start": v(803.27, 4483.1) * mm, "end": v(803.27, 5092.7) * mm});
            skLineSegment(sketch, "E8.18.8.3", {"start": v(806.45, 4635.5) * mm, "end": v(1416.05, 4635.5) * mm});
            skLineSegment(sketch, "E8.21.8.3", {"start": v(958.85, 5248.27) * mm, "end": v(806.45, 5248.27) * mm});
            skLineSegment(sketch, "E8.24.8.3", {"start": v(650.87, 4483.1) * mm, "end": v(650.87, 5092.7) * mm});
            skLineSegment(sketch, "E8.27.8.3", {"start": v(806.45, 4638.67) * mm, "end": v(806.45, 5248.27) * mm});
            skLineSegment(sketch, "E8.30.8.3", {"start": v(1260.47, 4327.52) * mm, "end": v(1260.47, 4479.92) * mm});
            skLineSegment(sketch, "E8.33.8.3", {"start": v(958.85, 4638.67) * mm, "end": v(958.85, 5248.27) * mm});
            skLineSegment(sketch, "E8.36.8.3", {"start": v(650.87, 4327.52) * mm, "end": v(650.87, 4479.92) * mm});
            skLineSegment(sketch, "E8.39.8.3", {"start": v(803.27, 5092.7) * mm, "end": v(650.87, 5092.7) * mm});
            skLineSegment(sketch, "E8.42.8.3", {"start": v(1416.05, 4483.1) * mm, "end": v(1416.05, 4635.5) * mm});
            skLineSegment(sketch, "E8.45.8.3", {"start": v(650.87, 4479.92) * mm, "end": v(1260.47, 4479.92) * mm});
            skLineSegment(sketch, "E8.0.8.4", {"start": v(38.1, 4940.3) * mm, "end": v(647.7, 4940.3) * mm});
            skLineSegment(sketch, "E8.3.8.4", {"start": v(190.5, 5095.87) * mm, "end": v(38.1, 5095.87) * mm});
            skLineSegment(sketch, "E8.6.8.4", {"start": v(193.67, 5095.87) * mm, "end": v(193.67, 5248.27) * mm});
            skLineSegment(sketch, "E8.9.8.4", {"start": v(346.07, 5251.45) * mm, "end": v(193.67, 5251.45) * mm});
            skLineSegment(sketch, "E8.12.8.4", {"start": v(193.67, 5095.87) * mm, "end": v(803.27, 5095.87) * mm});
            skLineSegment(sketch, "E8.15.8.4", {"start": v(190.5, 5095.87) * mm, "end": v(190.5, 5705.47) * mm});
            skLineSegment(sketch, "E8.18.8.4", {"start": v(193.67, 5248.27) * mm, "end": v(803.27, 5248.27) * mm});
            skLineSegment(sketch, "E8.21.8.4", {"start": v(346.07, 5861.05) * mm, "end": v(193.67, 5861.05) * mm});
            skLineSegment(sketch, "E8.24.8.4", {"start": v(38.1, 5095.87) * mm, "end": v(38.1, 5705.47) * mm});
            skLineSegment(sketch, "E8.27.8.4", {"start": v(193.67, 5251.45) * mm, "end": v(193.67, 5861.05) * mm});
            skLineSegment(sketch, "E8.30.8.4", {"start": v(647.7, 4940.3) * mm, "end": v(647.7, 5092.7) * mm});
            skLineSegment(sketch, "E8.33.8.4", {"start": v(346.07, 5251.45) * mm, "end": v(346.07, 5861.05) * mm});
            skLineSegment(sketch, "E8.36.8.4", {"start": v(38.1, 4940.3) * mm, "end": v(38.1, 5092.7) * mm});
            skLineSegment(sketch, "E8.39.8.4", {"start": v(190.5, 5705.47) * mm, "end": v(38.1, 5705.47) * mm});
            skLineSegment(sketch, "E8.42.8.4", {"start": v(803.27, 5095.87) * mm, "end": v(803.27, 5248.27) * mm});
            skLineSegment(sketch, "E8.45.8.4", {"start": v(38.1, 5092.7) * mm, "end": v(647.7, 5092.7) * mm});
            skSolve(sketch);
        }
        {
            var Q0;
            Q0=qSketchRegion(id+"F0",true);
            extrude(context, id + "F1", {"entities" : qUnion([Q0]), "depth" : 6.35 * mm, "offsetDistance" : 25.4 * mm});
        }
        {
            var Q0;
            Q0=qCreatedBy(makeId("Top.planeOp"),FACE);
            var sketch = newSketch(context, id + "F2", { "sketchPlane" : qUnion([Q0])});
            skLineSegment(sketch, "E9", {"start": v(1329.39, 2302.53) * mm, "end": v(1329.39, 3858.28) * mm});
            skLineSegment(sketch, "E10", {"start": v(1329.39, 3858.28) * mm, "end": v(-493.06, 3858.28) * mm});
            skLineSegment(sketch, "E11", {"start": v(-493.06, 3858.28) * mm, "end": v(-493.06, 2302.53) * mm});
            skLineSegment(sketch, "E12", {"start": v(-493.06, 2302.53) * mm, "end": v(1329.39, 2302.53) * mm});
            skLineSegment(sketch, "E13.bottom", {"start": v(-4816.06, 8587.4) * mm, "end": v(6787.9, 8587.4) * mm});
            skLineSegment(sketch, "E13.top", {"start": v(-4816.06, -1489.72) * mm, "end": v(6787.9, -1489.72) * mm});
            skLineSegment(sketch, "E13.left", {"start": v(-4816.06, 8587.4) * mm, "end": v(-4816.06, -1489.72) * mm});
            skLineSegment(sketch, "E13.right", {"start": v(6787.9, 8587.4) * mm, "end": v(6787.9, -1489.72) * mm});
            skLineSegment(sketch, "E14", {"start": v(485.78, 3092.45) * mm, "end": v(330.2, 2936.87) * mm, "construction": true});
            skLineSegment(sketch, "E15", {"start": v(485.78, 2936.87) * mm, "end": v(641.35, 3092.45) * mm, "construction": true});
            skLineSegment(sketch, "E16", {"start": v(452.87, 3059.54) * mm, "end": v(530.66, 2981.76) * mm, "construction": true});
            skLineSegment(sketch, "E17", {"start": v(491.76, 3020.65) * mm, "end": v(1329.39, 3858.28) * mm, "construction": true});
            skSolve(sketch);
        }
        {
            var Q0;
            Q0=qSketchRegion(id+"F2",true);
            extrude(context, id + "F3", {"entities" : qUnion([Q0]), "operationType" : NewBodyOperationType.REMOVE, "endBound" : BoundingType.THROUGH_ALL, "depth" : 25.4 * mm, "offsetDistance" : 25.4 * mm});
        }
    });
